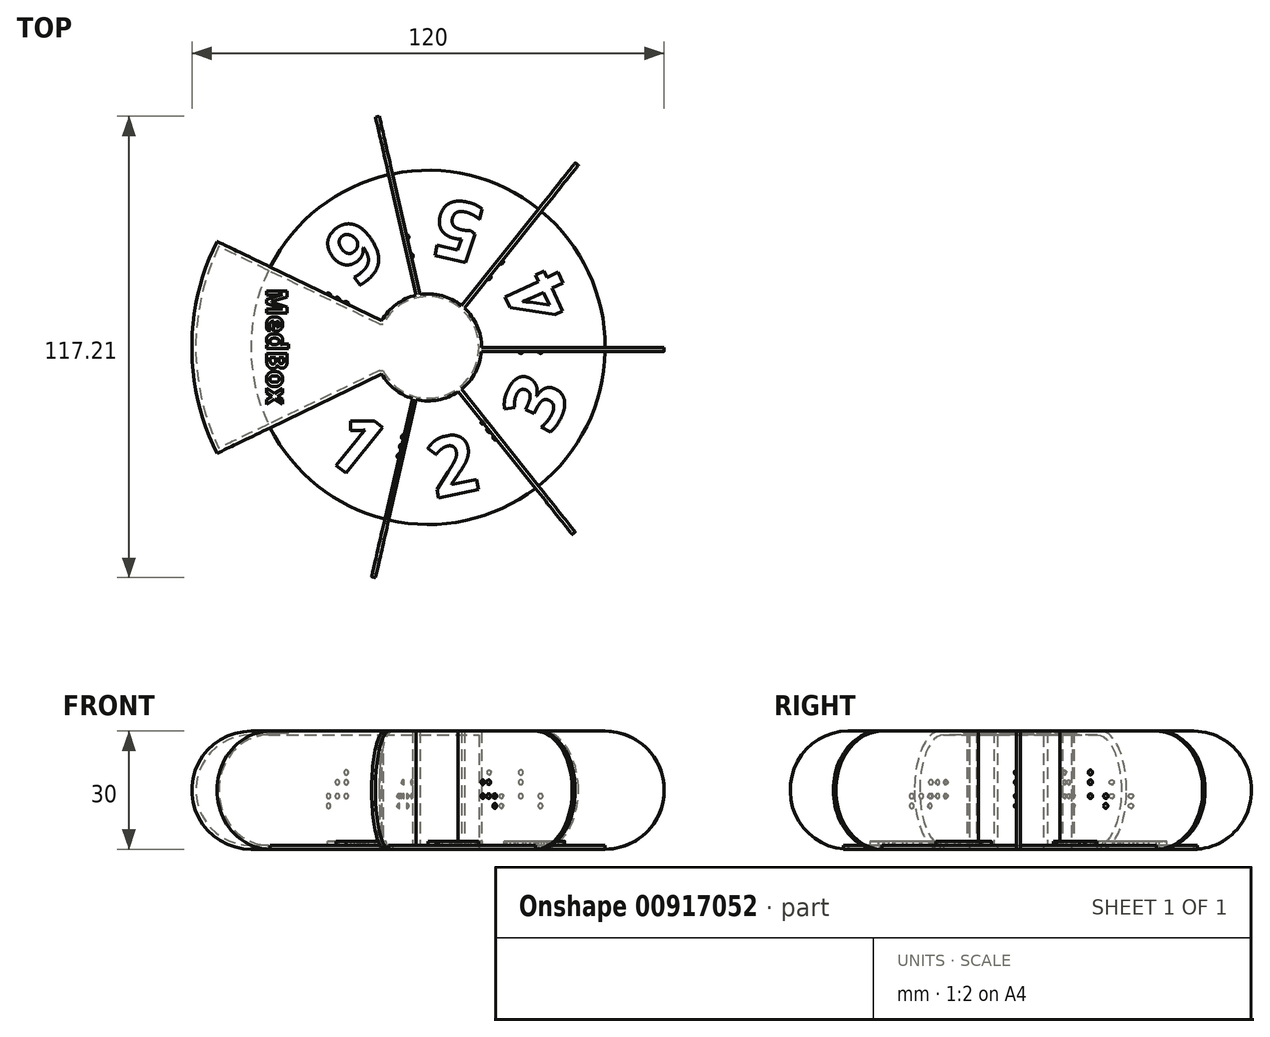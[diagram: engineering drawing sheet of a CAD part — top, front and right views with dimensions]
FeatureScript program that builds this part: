
annotation { "Feature Type Name" : "Feature", "Feature Type Description" : "" }
export const myFeature = defineFeature(function(context is Context, id is Id, definition is map)
    precondition{}
    {
        {
            var Q0;
            Q0=qCreatedBy(makeId("Top.planeOp"),FACE);
            var sketch = newSketch(context, id + "F0", { "sketchPlane" : qUnion([Q0])});
            skCircle(sketch, "E0", {"center": v(0, 0) * mm, "radius": 13.6 * mm});
            skCircle(sketch, "E1", {"center": v(0, 0) * mm, "radius": 60 * mm});
            skLineSegment(sketch, "E2", {"start": v(-3.03, 13.26) * mm, "end": v(-13.35, 58.5) * mm});
            skLineSegment(sketch, "E3", {"start": v(8.48, 10.63) * mm, "end": v(37.4, 46.9) * mm});
            skLineSegment(sketch, "E4", {"start": v(13.6, 0) * mm, "end": v(60, 0) * mm});
            skLineSegment(sketch, "E5", {"start": v(8.48, -10.63) * mm, "end": v(37.4, -46.9) * mm});
            skLineSegment(sketch, "E6", {"start": v(-3.03, -13.26) * mm, "end": v(-13.35, -58.5) * mm});
            skLineSegment(sketch, "E7", {"start": v(-12.25, -5.9) * mm, "end": v(-54.06, -26.03) * mm});
            skLineSegment(sketch, "E8", {"start": v(-12.25, 5.9) * mm, "end": v(-54.06, 26.03) * mm});
            skLineSegment(sketch, "E9", {"start": v(-11.79, 6.79) * mm, "end": v(-53.62, 26.93) * mm});
            skLineSegment(sketch, "E10", {"start": v(-2.04, 13.45) * mm, "end": v(-12.37, 58.71) * mm});
            skLineSegment(sketch, "E11", {"start": v(9.24, 9.98) * mm, "end": v(38.19, 46.28) * mm});
            skLineSegment(sketch, "E12", {"start": v(13.56, -1) * mm, "end": v(60, -1) * mm});
            skLineSegment(sketch, "E13", {"start": v(7.67, -11.23) * mm, "end": v(36.62, -47.53) * mm});
            skLineSegment(sketch, "E14", {"start": v(-4, -13) * mm, "end": v(-14.32, -58.27) * mm});
            skLineSegment(sketch, "E15", {"start": v(-11.79, -6.79) * mm, "end": v(-53.62, -26.93) * mm});
            skSolve(sketch);
        }
        {
            var Q0;
            {var subQ0=sQuery(id+"F0.wireOp",EDGE,"E8");Q0=makeQuery(id+"F0.imprint","IMPRINT",FACE,{"disambiguationData":[TD([[makeQuery(id+"F0.imprint","IMPRINT",EDGE,{"derivedFrom":subQ0}),-1.0]])]});}
            var Q1;
            {var subQ0=sQuery(id+"F0.wireOp",EDGE,"E2");Q1=makeQuery(id+"F0.imprint","IMPRINT",FACE,{"disambiguationData":[TD([[makeQuery(id+"F0.imprint","IMPRINT",EDGE,{"derivedFrom":subQ0}),-1.0]])]});}
            var Q2;
            {var subQ0=sQuery(id+"F0.wireOp",EDGE,"E3");Q2=makeQuery(id+"F0.imprint","IMPRINT",FACE,{"disambiguationData":[TD([[makeQuery(id+"F0.imprint","IMPRINT",EDGE,{"derivedFrom":subQ0}),-1.0]])]});}
            var Q3;
            {var subQ0=sQuery(id+"F0.wireOp",EDGE,"E4");Q3=makeQuery(id+"F0.imprint","IMPRINT",FACE,{"disambiguationData":[TD([[makeQuery(id+"F0.imprint","IMPRINT",EDGE,{"derivedFrom":subQ0}),-1.0]])]});}
            var Q4;
            {var subQ0=sQuery(id+"F0.wireOp",EDGE,"E5");Q4=makeQuery(id+"F0.imprint","IMPRINT",FACE,{"disambiguationData":[TD([[makeQuery(id+"F0.imprint","IMPRINT",EDGE,{"derivedFrom":subQ0}),-1.0]])]});}
            var Q5;
            {var subQ0=sQuery(id+"F0.wireOp",EDGE,"E6");Q5=makeQuery(id+"F0.imprint","IMPRINT",FACE,{"disambiguationData":[TD([[makeQuery(id+"F0.imprint","IMPRINT",EDGE,{"derivedFrom":subQ0}),-1.0]])]});}
            var Q6;
            {var subQ0=sQuery(id+"F0.wireOp",EDGE,"E7");Q6=makeQuery(id+"F0.imprint","IMPRINT",FACE,{"disambiguationData":[TD([[makeQuery(id+"F0.imprint","IMPRINT",EDGE,{"derivedFrom":subQ0}),1.0]])]});}
            var Q7;
            {var subQ0=sQuery(id+"F0.wireOp",EDGE,"E0");var subQ8=makeQuery(id+"F0.imprint","INTERSECT",VERTEX,{"derivedFrom":[subQ0,sQuery(id+"F0.wireOp",EDGE,"E4")]});Q7=makeQuery(id+"F0.imprint","IMPRINT",FACE,{"disambiguationData":[TD([[makeQuery(id+"F0.imprint","IMPRINT",EDGE,{"disambiguationData":[TD([[subQ8,-1.0]])],"derivedFrom":subQ0}),1.0]])]});}
            extrude(context, id + "F1", {"entities" : qUnion([Q0, Q1, Q2, Q3, Q4, Q5, Q6, Q7]), "depth" : 30 * mm, "offsetDistance" : 25 * mm});
        }
        {
            var Q0;
            {var subQ0=sQuery(id+"F0.wireOp",EDGE,"E1");Q0=makeQuery(id+"F1.opExtrude","CAP_EDGE",EDGE,{"disambiguationData":[OSD([subQ0]),TDD([makeQuery(id+"F0.imprint","IMPRINT",EDGE,{"disambiguationData":[TD([[makeQuery(id+"F0.imprint","INTERSECT",VERTEX,{"derivedFrom":[subQ0,sQuery(id+"F0.wireOp",EDGE,"E7")]}),-1.0]])],"derivedFrom":subQ0})])],"isStart":false});}
            var Q1;
            {var subQ0=sQuery(id+"F0.wireOp",EDGE,"E1");Q1=makeQuery(id+"F1.opExtrude","CAP_EDGE",EDGE,{"disambiguationData":[OSD([subQ0]),TDD([makeQuery(id+"F0.imprint","IMPRINT",EDGE,{"disambiguationData":[TD([[makeQuery(id+"F0.imprint","INTERSECT",VERTEX,{"derivedFrom":[subQ0,sQuery(id+"F0.wireOp",EDGE,"E6")]}),1.0]])],"derivedFrom":subQ0})])],"isStart":false});}
            var Q2;
            {var subQ0=sQuery(id+"F0.wireOp",EDGE,"E1");Q2=makeQuery(id+"F1.opExtrude","CAP_EDGE",EDGE,{"disambiguationData":[OSD([subQ0]),TDD([makeQuery(id+"F0.imprint","IMPRINT",EDGE,{"disambiguationData":[TD([[makeQuery(id+"F0.imprint","INTERSECT",VERTEX,{"derivedFrom":[subQ0,sQuery(id+"F0.wireOp",EDGE,"E5")]}),1.0]])],"derivedFrom":subQ0})])],"isStart":false});}
            var Q3;
            {var subQ0=sQuery(id+"F0.wireOp",EDGE,"E1");Q3=makeQuery(id+"F1.opExtrude","CAP_EDGE",EDGE,{"disambiguationData":[OSD([subQ0]),TDD([makeQuery(id+"F0.imprint","IMPRINT",EDGE,{"disambiguationData":[TD([[makeQuery(id+"F0.imprint","INTERSECT",VERTEX,{"derivedFrom":[subQ0,sQuery(id+"F0.wireOp",EDGE,"E4")]}),1.0]])],"derivedFrom":subQ0})])],"isStart":false});}
            var Q4;
            {var subQ0=sQuery(id+"F0.wireOp",EDGE,"E1");Q4=makeQuery(id+"F1.opExtrude","CAP_EDGE",EDGE,{"disambiguationData":[OSD([subQ0]),TDD([makeQuery(id+"F0.imprint","IMPRINT",EDGE,{"disambiguationData":[TD([[makeQuery(id+"F0.imprint","INTERSECT",VERTEX,{"derivedFrom":[subQ0,sQuery(id+"F0.wireOp",EDGE,"E3")]}),1.0]])],"derivedFrom":subQ0})])],"isStart":false});}
            var Q5;
            {var subQ0=sQuery(id+"F0.wireOp",EDGE,"E1");Q5=makeQuery(id+"F1.opExtrude","CAP_EDGE",EDGE,{"disambiguationData":[OSD([subQ0]),TDD([makeQuery(id+"F0.imprint","IMPRINT",EDGE,{"disambiguationData":[TD([[makeQuery(id+"F0.imprint","INTERSECT",VERTEX,{"derivedFrom":[subQ0,sQuery(id+"F0.wireOp",EDGE,"E2")]}),1.0]])],"derivedFrom":subQ0})])],"isStart":false});}
            var Q6;
            {var subQ0=sQuery(id+"F0.wireOp",EDGE,"E1");Q6=makeQuery(id+"F1.opExtrude","CAP_EDGE",EDGE,{"disambiguationData":[OSD([subQ0]),TDD([makeQuery(id+"F0.imprint","IMPRINT",EDGE,{"disambiguationData":[TD([[makeQuery(id+"F0.imprint","INTERSECT",VERTEX,{"derivedFrom":[subQ0,sQuery(id+"F0.wireOp",EDGE,"E8")]}),1.0]])],"derivedFrom":subQ0})])],"isStart":false});}
            var Q7;
            {var subQ0=sQuery(id+"F0.wireOp",EDGE,"E1");Q7=makeQuery(id+"F1.opExtrude","CAP_EDGE",EDGE,{"disambiguationData":[OSD([subQ0]),TDD([makeQuery(id+"F0.imprint","IMPRINT",EDGE,{"disambiguationData":[TD([[makeQuery(id+"F0.imprint","INTERSECT",VERTEX,{"derivedFrom":[subQ0,sQuery(id+"F0.wireOp",EDGE,"E6")]}),1.0]])],"derivedFrom":subQ0})])],"isStart":true});}
            var Q8;
            {var subQ0=sQuery(id+"F0.wireOp",EDGE,"E1");Q8=makeQuery(id+"F1.opExtrude","CAP_EDGE",EDGE,{"disambiguationData":[OSD([subQ0]),TDD([makeQuery(id+"F0.imprint","IMPRINT",EDGE,{"disambiguationData":[TD([[makeQuery(id+"F0.imprint","INTERSECT",VERTEX,{"derivedFrom":[subQ0,sQuery(id+"F0.wireOp",EDGE,"E5")]}),1.0]])],"derivedFrom":subQ0})])],"isStart":true});}
            var Q9;
            {var subQ0=sQuery(id+"F0.wireOp",EDGE,"E1");Q9=makeQuery(id+"F1.opExtrude","CAP_EDGE",EDGE,{"disambiguationData":[OSD([subQ0]),TDD([makeQuery(id+"F0.imprint","IMPRINT",EDGE,{"disambiguationData":[TD([[makeQuery(id+"F0.imprint","INTERSECT",VERTEX,{"derivedFrom":[subQ0,sQuery(id+"F0.wireOp",EDGE,"E7")]}),-1.0]])],"derivedFrom":subQ0})])],"isStart":true});}
            var Q10;
            {var subQ0=sQuery(id+"F0.wireOp",EDGE,"E1");Q10=makeQuery(id+"F1.opExtrude","CAP_EDGE",EDGE,{"disambiguationData":[OSD([subQ0]),TDD([makeQuery(id+"F0.imprint","IMPRINT",EDGE,{"disambiguationData":[TD([[makeQuery(id+"F0.imprint","INTERSECT",VERTEX,{"derivedFrom":[subQ0,sQuery(id+"F0.wireOp",EDGE,"E8")]}),1.0]])],"derivedFrom":subQ0})])],"isStart":true});}
            var Q11;
            {var subQ0=sQuery(id+"F0.wireOp",EDGE,"E1");Q11=makeQuery(id+"F1.opExtrude","CAP_EDGE",EDGE,{"disambiguationData":[OSD([subQ0]),TDD([makeQuery(id+"F0.imprint","IMPRINT",EDGE,{"disambiguationData":[TD([[makeQuery(id+"F0.imprint","INTERSECT",VERTEX,{"derivedFrom":[subQ0,sQuery(id+"F0.wireOp",EDGE,"E4")]}),1.0]])],"derivedFrom":subQ0})])],"isStart":true});}
            var Q12;
            {var subQ0=sQuery(id+"F0.wireOp",EDGE,"E1");Q12=makeQuery(id+"F1.opExtrude","CAP_EDGE",EDGE,{"disambiguationData":[OSD([subQ0]),TDD([makeQuery(id+"F0.imprint","IMPRINT",EDGE,{"disambiguationData":[TD([[makeQuery(id+"F0.imprint","INTERSECT",VERTEX,{"derivedFrom":[subQ0,sQuery(id+"F0.wireOp",EDGE,"E2")]}),1.0]])],"derivedFrom":subQ0})])],"isStart":true});}
            var Q13;
            {var subQ0=sQuery(id+"F0.wireOp",EDGE,"E1");Q13=makeQuery(id+"F1.opExtrude","CAP_EDGE",EDGE,{"disambiguationData":[OSD([subQ0]),TDD([makeQuery(id+"F0.imprint","IMPRINT",EDGE,{"disambiguationData":[TD([[makeQuery(id+"F0.imprint","INTERSECT",VERTEX,{"derivedFrom":[subQ0,sQuery(id+"F0.wireOp",EDGE,"E3")]}),1.0]])],"derivedFrom":subQ0})])],"isStart":true});}
            fillet(context, id + "F2", {"entities" : qUnion([Q0, Q1, Q2, Q3, Q4, Q5, Q6, Q7, Q8, Q9, Q10, Q11, Q12, Q13]), "radius" : 15 * mm, "tangentPropagation" : true, "allowEdgeOverflow" : false});
        }
        {
            var Q0;
            Q0=makeQuery(id+"F1.opExtrude","SWEPT_FACE",FACE,{"disambiguationData":[OSD([sQuery(id+"F0.wireOp",EDGE,"E8")])]});
            var sketch = newSketch(context, id + "F3", { "sketchPlane" : qUnion([Q0])});
            skLineSegment(sketch, "E16", {"start": v(0, 0) * mm, "end": v(0, 50) * mm});
            skLineSegment(sketch, "E17", {"start": v(-13.6, 0) * mm, "end": v(-13.6, 1) * mm});
            skLineSegment(sketch, "E18", {"start": v(-13.6, 30) * mm, "end": v(-13.6, 29) * mm});
            skLineSegment(sketch, "E19", {"start": v(-45, 30) * mm, "end": v(-45, 29) * mm});
            skLineSegment(sketch, "E20", {"start": v(-45, 0) * mm, "end": v(-45, 1) * mm});
            skArc(sketch, "E21", {"start": v(-45, 29) * mm, "mid": v(-59, 15) * mm, "end": v(-45, 1) * mm});
            skLineSegment(sketch, "E22", {"start": v(-45, 29) * mm, "end": v(-13.6, 29) * mm});
            skLineSegment(sketch, "E23", {"start": v(-45, 1) * mm, "end": v(-13.6, 1) * mm});
            skSolve(sketch);
        }
        {
            var Q0;
            Q0=makeQuery(id+"F3.imprint","IMPRINT",FACE,{"disambiguationData":[TD([[makeQuery(id+"F3.imprint","IMPRINT",EDGE,{"derivedFrom":sQuery(id+"F3.wireOp",EDGE,"E18")}),-1.0]])]});
            var Q1;
            Q1=makeQuery(id+"F3.imprint","IMPRINT",FACE,{"disambiguationData":[TD([[makeQuery(id+"F3.imprint","IMPRINT",EDGE,{"derivedFrom":sQuery(id+"F3.wireOp",EDGE,"E19")}),-1.0]])]});
            var Q2;
            Q2=sQuery(id+"F3.wireOp",EDGE,"E16");
            revolve(context, id + "F4", {"operationType" : NewBodyOperationType.ADD, "surfaceOperationType" : NewSurfaceOperationType.NEW, "entities" : qUnion([Q0, Q1]), "axis" : qUnion([Q2]), "revolveType" : RevolveType.ONE_DIRECTION, "angle" : 52 * degree});
        }
        {
            var Q0;
            Q0=makeQuery(id+"F1.opExtrude","CAP_FACE",FACE,{"disambiguationData":[OSD([sQuery(id+"F0.wireOp",EDGE,"E0"),sQuery(id+"F0.wireOp",EDGE,"E1"),sQuery(id+"F0.wireOp",EDGE,"E2"),sQuery(id+"F0.wireOp",EDGE,"E3"),sQuery(id+"F0.wireOp",EDGE,"E4"),sQuery(id+"F0.wireOp",EDGE,"E5"),sQuery(id+"F0.wireOp",EDGE,"E6"),sQuery(id+"F0.wireOp",EDGE,"E7"),sQuery(id+"F0.wireOp",EDGE,"E8"),sQuery(id+"F0.wireOp",EDGE,"E9"),sQuery(id+"F0.wireOp",EDGE,"E10"),sQuery(id+"F0.wireOp",EDGE,"E11"),sQuery(id+"F0.wireOp",EDGE,"E12"),sQuery(id+"F0.wireOp",EDGE,"E13"),sQuery(id+"F0.wireOp",EDGE,"E14"),sQuery(id+"F0.wireOp",EDGE,"E15")])],"isStart":true});
            var sketch = newSketch(context, id + "F5", { "sketchPlane" : qUnion([Q0])});
            skCircle(sketch, "E24", {"center": v(0, 0) * mm, "radius": 12.9 * mm});
            skLineSegment(sketch, "E25", {"start": v(-12.25, 5.9) * mm, "end": v(-11.47, 5.9) * mm});
            skLineSegment(sketch, "E26", {"start": v(-12.25, -5.9) * mm, "end": v(-11.47, -5.9) * mm});
            skSolve(sketch);
        }
        {
            var Q0;
            {var subQ0=sQuery(id+"F5.wireOp",EDGE,"E24");var subQ1=makeQuery(id+"F5.imprint","INTERSECT",VERTEX,{"derivedFrom":[subQ0,sQuery(id+"F5.wireOp",EDGE,"E25")]});Q0=makeQuery(id+"F5.imprint","IMPRINT",FACE,{"disambiguationData":[TD([[makeQuery(id+"F5.imprint","IMPRINT",EDGE,{"disambiguationData":[TD([[subQ1,-1.0]])],"derivedFrom":subQ0}),1.0]])]});}
            var Q1;
            {var subQ0=sQuery(id+"F5.wireOp",EDGE,"E25");Q1=makeQuery(id+"F5.imprint","IMPRINT",FACE,{"disambiguationData":[TD([[makeQuery(id+"F5.imprint","IMPRINT",EDGE,{"derivedFrom":subQ0}),-1.0]])]});}
            extrude(context, id + "F6", {"entities" : qUnion([Q0, Q1]), "operationType" : NewBodyOperationType.REMOVE, "oppositeDirection" : true, "depth" : 29 * mm, "offsetDistance" : 25 * mm});
        }
        {
            var Q0;
            Q0=makeQuery(id+"F1.opExtrude","CAP_FACE",FACE,{"disambiguationData":[OSD([sQuery(id+"F0.wireOp",EDGE,"E0"),sQuery(id+"F0.wireOp",EDGE,"E1"),sQuery(id+"F0.wireOp",EDGE,"E2"),sQuery(id+"F0.wireOp",EDGE,"E3"),sQuery(id+"F0.wireOp",EDGE,"E4"),sQuery(id+"F0.wireOp",EDGE,"E5"),sQuery(id+"F0.wireOp",EDGE,"E6"),sQuery(id+"F0.wireOp",EDGE,"E7"),sQuery(id+"F0.wireOp",EDGE,"E8"),sQuery(id+"F0.wireOp",EDGE,"E9"),sQuery(id+"F0.wireOp",EDGE,"E10"),sQuery(id+"F0.wireOp",EDGE,"E11"),sQuery(id+"F0.wireOp",EDGE,"E12"),sQuery(id+"F0.wireOp",EDGE,"E13"),sQuery(id+"F0.wireOp",EDGE,"E14"),sQuery(id+"F0.wireOp",EDGE,"E15")])],"isStart":true});
            var sketch = newSketch(context, id + "F7", { "sketchPlane" : qUnion([Q0])});
            skArc(sketch, "E27", {"start": v(-40.54, 19.52) * mm, "mid": v(45, 0) * mm, "end": v(-40.54, -19.52) * mm});
            skSolve(sketch);
        }
        {
            var Q0;
            {var subQ3=sQuery(id+"F0.wireOp",EDGE,"E14");var subQ4=makeQuery(id+"F1.opExtrude","CAP_EDGE",EDGE,{"disambiguationData":[OSD([subQ3])],"isStart":true});Q0=makeQuery(id+"F7.imprint","IMPRINT",FACE,{"disambiguationData":[TD([[makeQuery(id+"F7.imprint","IMPRINT",EDGE,{"derivedFrom":subQ4}),1.0]])]});}
            var Q1;
            {var subQ1=sQuery(id+"F0.wireOp",EDGE,"E6");var subQ2=makeQuery(id+"F1.opExtrude","CAP_EDGE",EDGE,{"disambiguationData":[OSD([subQ1])],"isStart":true});Q1=makeQuery(id+"F7.imprint","IMPRINT",FACE,{"disambiguationData":[TD([[makeQuery(id+"F7.imprint","IMPRINT",EDGE,{"derivedFrom":subQ2}),-1.0]])]});}
            var Q2;
            {var subQ1=sQuery(id+"F0.wireOp",EDGE,"E5");var subQ2=makeQuery(id+"F1.opExtrude","CAP_EDGE",EDGE,{"disambiguationData":[OSD([subQ1])],"isStart":true});Q2=makeQuery(id+"F7.imprint","IMPRINT",FACE,{"disambiguationData":[TD([[makeQuery(id+"F7.imprint","IMPRINT",EDGE,{"derivedFrom":subQ2}),-1.0]])]});}
            var Q3;
            {var subQ3=sQuery(id+"F0.wireOp",EDGE,"E4");var subQ4=makeQuery(id+"F1.opExtrude","CAP_EDGE",EDGE,{"disambiguationData":[OSD([subQ3])],"isStart":true});Q3=makeQuery(id+"F7.imprint","IMPRINT",FACE,{"disambiguationData":[TD([[makeQuery(id+"F7.imprint","IMPRINT",EDGE,{"derivedFrom":subQ4}),-1.0]])]});}
            var Q4;
            {var subQ1=sQuery(id+"F0.wireOp",EDGE,"E3");var subQ2=makeQuery(id+"F1.opExtrude","CAP_EDGE",EDGE,{"disambiguationData":[OSD([subQ1])],"isStart":true});Q4=makeQuery(id+"F7.imprint","IMPRINT",FACE,{"disambiguationData":[TD([[makeQuery(id+"F7.imprint","IMPRINT",EDGE,{"derivedFrom":subQ2}),-1.0]])]});}
            var Q5;
            {var subQ1=sQuery(id+"F0.wireOp",EDGE,"E2");var subQ2=makeQuery(id+"F1.opExtrude","CAP_EDGE",EDGE,{"disambiguationData":[OSD([subQ1])],"isStart":true});Q5=makeQuery(id+"F7.imprint","IMPRINT",FACE,{"disambiguationData":[TD([[makeQuery(id+"F7.imprint","IMPRINT",EDGE,{"derivedFrom":subQ2}),-1.0]])]});}
            extrude(context, id + "F8", {"entities" : qUnion([Q0, Q1, Q2, Q3, Q4, Q5]), "operationType" : NewBodyOperationType.ADD, "oppositeDirection" : true, "depth" : 1 * mm, "offsetDistance" : 25 * mm});
        }
        {
            var Q0;
            Q0=makeQuery(id+"F8.opExtrude","CAP_FACE",FACE,{"disambiguationData":[OSD([sQuery(id+"F0.wireOp",EDGE,"E0"),sQuery(id+"F0.wireOp",EDGE,"E14"),sQuery(id+"F0.wireOp",EDGE,"E15"),sQuery(id+"F7.wireOp",EDGE,"E27")])],"isStart":false});
            var sketch = newSketch(context, id + "F9", { "sketchPlane" : qUnion([Q0])});
            skCircle(sketch, "E28", {"center": v(0, 0) * mm, "radius": 23 * mm});
            skLineSegment(sketch, "E29", {"start": v(0, 0) * mm, "end": v(40.32, -19.97) * mm});
            skLineSegment(sketch, "E30", {"start": v(0, 0) * mm, "end": v(40.76, 19.07) * mm});
            skLineSegment(sketch, "E31", {"start": v(0, 0) * mm, "end": v(10.5, 43.76) * mm});
            skLineSegment(sketch, "E32", {"start": v(0, 0) * mm, "end": v(-27.66, 35.5) * mm});
            skLineSegment(sketch, "E33", {"start": v(0, 0) * mm, "end": v(9.53, -43.98) * mm});
            skText(sketch, "E34", { "text": "2", "fontName": "OpenSans-Bold.ttf"});
            skLineSegment(sketch, "E35", {"start": v(0, 0) * mm, "end": v(-28.06, -35.18) * mm});
            skText(sketch, "E36", { "text": "1", "fontName": "OpenSans-Bold.ttf"});
            skText(sketch, "E37", { "text": "3", "fontName": "OpenSans-Bold.ttf"});
            skText(sketch, "E38", { "text": "4", "fontName": "OpenSans-Bold.ttf"});
            skText(sketch, "E39", { "text": "5", "fontName": "OpenSans-Bold.ttf"});
            skText(sketch, "E40", { "text": "6", "fontName": "OpenSans-Bold.ttf"});
            const initialGuessF9  = {"E34": [0.0019, -0.03847, 0.97734, 0.21167, 0.015], "E36": [-0.02759, -0.0266, 0.78183, -0.62349, 0.015], "E37": [0.0313, -0.02244, 0.44387, 0.8961, 0.015], "E38": [0.03716, 0.01026, -0.42385, 0.90573, 0.015], "E39": [0.01485, 0.03552, -0.9724, 0.23334, 0.015], "E40": [-0.0184, 0.03384, -0.78871, -0.61476, 0.015]};
            skSetInitialGuess(sketch, initialGuessF9);
            skSolve(sketch);
        }
        {
            var Q0;
            {var subQ0=sQuery(id+"F9.wireOp",EDGE,"E39.sketch_text.stroke-4");Q0=makeQuery(id+"F9.imprint","IMPRINT",FACE,{"disambiguationData":[TD([[makeQuery(id+"F9.imprint","IMPRINT",EDGE,{"derivedFrom":subQ0}),-1.0]])]});}
            var Q1;
            {var subQ5=sQuery(id+"F9.wireOp",EDGE,"E39.sketch_text.stroke-0");Q1=makeQuery(id+"F9.imprint","IMPRINT",FACE,{"disambiguationData":[TD([[makeQuery(id+"F9.imprint","IMPRINT",EDGE,{"derivedFrom":subQ5}),-1.0]])]});}
            var Q2;
            {var subQ11=sQuery(id+"F9.wireOp",EDGE,"E39.sketch_text.stroke-10");Q2=makeQuery(id+"F9.imprint","IMPRINT",FACE,{"disambiguationData":[TD([[makeQuery(id+"F9.imprint","IMPRINT",EDGE,{"derivedFrom":subQ11}),-1.0]])]});}
            var Q3;
            {var subQ5=sQuery(id+"F9.wireOp",EDGE,"E39.sketch_text.stroke-15");Q3=makeQuery(id+"F9.imprint","IMPRINT",FACE,{"disambiguationData":[TD([[makeQuery(id+"F9.imprint","IMPRINT",EDGE,{"derivedFrom":subQ5}),-1.0]])]});}
            var Q4;
            Q4=makeQuery(id+"F9.imprint","IMPRINT",FACE,{"disambiguationData":[TD([[makeQuery(id+"F9.imprint","IMPRINT",EDGE,{"derivedFrom":sQuery(id+"F9.wireOp",EDGE,"E38.sketch_text.stroke-0")}),-1.0]])]});
            var Q5;
            {var subQ0=sQuery(id+"F9.wireOp",EDGE,"E38.sketch_text.stroke-5");Q5=makeQuery(id+"F9.imprint","IMPRINT",FACE,{"disambiguationData":[TD([[makeQuery(id+"F9.imprint","IMPRINT",EDGE,{"derivedFrom":subQ0}),-1.0]])]});}
            var Q6;
            Q6=makeQuery(id+"F9.imprint","IMPRINT",FACE,{"disambiguationData":[TD([[makeQuery(id+"F9.imprint","IMPRINT",EDGE,{"derivedFrom":sQuery(id+"F9.wireOp",EDGE,"E37.sketch_text.stroke-0")}),-1.0]])]});
            var Q7;
            {var subQ0=sQuery(id+"F9.wireOp",EDGE,"E37.sketch_text.stroke-21");Q7=makeQuery(id+"F9.imprint","IMPRINT",FACE,{"disambiguationData":[TD([[makeQuery(id+"F9.imprint","IMPRINT",EDGE,{"derivedFrom":subQ0}),-1.0]])]});}
            var Q8;
            {var subQ0=sQuery(id+"F9.wireOp",EDGE,"E37.sketch_text.stroke-15");Q8=makeQuery(id+"F9.imprint","IMPRINT",FACE,{"disambiguationData":[TD([[makeQuery(id+"F9.imprint","IMPRINT",EDGE,{"derivedFrom":subQ0}),-1.0]])]});}
            var Q9;
            {var subQ0=sQuery(id+"F9.wireOp",EDGE,"E37.sketch_text.stroke-7");Q9=makeQuery(id+"F9.imprint","IMPRINT",FACE,{"disambiguationData":[TD([[makeQuery(id+"F9.imprint","IMPRINT",EDGE,{"derivedFrom":subQ0}),-1.0]])]});}
            var Q10;
            {var subQ0=sQuery(id+"F9.wireOp",EDGE,"E34.sketch_text.stroke-1");Q10=makeQuery(id+"F9.imprint","IMPRINT",FACE,{"disambiguationData":[TD([[makeQuery(id+"F9.imprint","IMPRINT",EDGE,{"derivedFrom":subQ0}),-1.0]])]});}
            var Q11;
            {var subQ5=sQuery(id+"F9.wireOp",EDGE,"E34.sketch_text.stroke-23");Q11=makeQuery(id+"F9.imprint","IMPRINT",FACE,{"disambiguationData":[TD([[makeQuery(id+"F9.imprint","IMPRINT",EDGE,{"derivedFrom":subQ5}),-1.0]])]});}
            var Q12;
            {var subQ13=sQuery(id+"F9.wireOp",EDGE,"E34.sketch_text.stroke-4");Q12=makeQuery(id+"F9.imprint","IMPRINT",FACE,{"disambiguationData":[TD([[makeQuery(id+"F9.imprint","IMPRINT",EDGE,{"derivedFrom":subQ13}),-1.0]])]});}
            var Q13;
            {var subQ0=sQuery(id+"F9.wireOp",EDGE,"E34.sketch_text.stroke-8");Q13=makeQuery(id+"F9.imprint","IMPRINT",FACE,{"disambiguationData":[TD([[makeQuery(id+"F9.imprint","IMPRINT",EDGE,{"derivedFrom":subQ0}),-1.0]])]});}
            var Q14;
            {var subQ1=sQuery(id+"F9.wireOp",EDGE,"E36.sketch_text.stroke-5");Q14=makeQuery(id+"F9.imprint","IMPRINT",FACE,{"disambiguationData":[TD([[makeQuery(id+"F9.imprint","IMPRINT",EDGE,{"derivedFrom":subQ1}),-1.0]])]});}
            var Q15;
            Q15=makeQuery(id+"F9.imprint","IMPRINT",FACE,{"disambiguationData":[TD([[makeQuery(id+"F9.imprint","IMPRINT",EDGE,{"derivedFrom":sQuery(id+"F9.wireOp",EDGE,"E36.sketch_text.stroke-0")}),-1.0]])]});
            var Q16;
            {var subQ11=sQuery(id+"F9.wireOp",EDGE,"E40.sketch_text.stroke-0");Q16=makeQuery(id+"F9.imprint","IMPRINT",FACE,{"disambiguationData":[TD([[makeQuery(id+"F9.imprint","IMPRINT",EDGE,{"derivedFrom":subQ11}),-1.0]])]});}
            var Q17;
            {var subQ8=sQuery(id+"F9.wireOp",EDGE,"E40.sketch_text.stroke-10");Q17=makeQuery(id+"F9.imprint","IMPRINT",FACE,{"disambiguationData":[TD([[makeQuery(id+"F9.imprint","IMPRINT",EDGE,{"derivedFrom":subQ8}),-1.0]])]});}
            var Q18;
            {var subQ0=sQuery(id+"F9.wireOp",EDGE,"E40.sketch_text.stroke-2");Q18=makeQuery(id+"F9.imprint","IMPRINT",FACE,{"disambiguationData":[TD([[makeQuery(id+"F9.imprint","IMPRINT",EDGE,{"derivedFrom":subQ0}),-1.0]])]});}
            extrude(context, id + "F10", {"entities" : qUnion([Q0, Q1, Q2, Q3, Q4, Q5, Q6, Q7, Q8, Q9, Q10, Q11, Q12, Q13, Q14, Q15, Q16, Q17, Q18]), "operationType" : NewBodyOperationType.ADD, "depth" : 1 * mm, "offsetDistance" : 25 * mm});
        }
        {
            var Q0;
            Q0=makeQuery(id+"F1.opExtrude","SWEPT_FACE",FACE,{"disambiguationData":[OSD([sQuery(id+"F0.wireOp",EDGE,"E14")])]});
            var sketch = newSketch(context, id + "F11", { "sketchPlane" : qUnion([Q0])});
            skLineSegment(sketch, "E41", {"start": v(23.56, 19.5) * mm, "end": v(23.56, 11) * mm});
            skLineSegment(sketch, "E42", {"start": v(23.56, 11) * mm, "end": v(28.56, 11) * mm});
            skCircle(sketch, "E43", {"center": v(23.56, 11) * mm, "radius": 0.6 * mm});
            skPoint(sketch, "E44", {"position": v(23.56, 13.5) * mm});
            skCircle(sketch, "E45", {"center": v(23.56, 13.5) * mm, "radius": 0.6 * mm});
            skPoint(sketch, "E46", {"position": v(23.56, 17) * mm});
            skCircle(sketch, "E47", {"center": v(23.56, 17) * mm, "radius": 0.6 * mm});
            skCircle(sketch, "E48", {"center": v(23.56, 19.5) * mm, "radius": 0.6 * mm});
            skPoint(sketch, "E49", {"position": v(26.06, 11) * mm});
            skCircle(sketch, "E50", {"center": v(26.06, 11) * mm, "radius": 0.6 * mm});
            skCircle(sketch, "E51", {"center": v(28.56, 11) * mm, "radius": 0.6 * mm});
            skLineSegment(sketch, "E52", {"start": v(23.56, 13.5) * mm, "end": v(28.56, 13.5) * mm});
            skCircle(sketch, "E53", {"center": v(26.06, 13.5) * mm, "radius": 0.6 * mm});
            skCircle(sketch, "E54", {"center": v(28.56, 13.5) * mm, "radius": 0.6 * mm});
            skLineSegment(sketch, "E55", {"start": v(23.56, 17) * mm, "end": v(28.56, 17) * mm});
            skCircle(sketch, "E56", {"center": v(26.06, 17) * mm, "radius": 0.6 * mm});
            skCircle(sketch, "E57", {"center": v(28.56, 17) * mm, "radius": 0.6 * mm});
            skLineSegment(sketch, "E58", {"start": v(23.56, 19.5) * mm, "end": v(28.56, 19.5) * mm});
            skCircle(sketch, "E59", {"center": v(26.06, 19.5) * mm, "radius": 0.6 * mm});
            skCircle(sketch, "E60", {"center": v(28.56, 19.5) * mm, "radius": 0.6 * mm});
            skSolve(sketch);
        }
        {
            var Q0;
            Q0=makeQuery(id+"F1.opExtrude","SWEPT_FACE",FACE,{"disambiguationData":[OSD([sQuery(id+"F0.wireOp",EDGE,"E13")])]});
            var sketch = newSketch(context, id + "F12", { "sketchPlane" : qUnion([Q0])});
            skLineSegment(sketch, "E61", {"start": v(23.56, 19.5) * mm, "end": v(23.56, 11) * mm});
            skLineSegment(sketch, "E62", {"start": v(23.56, 11) * mm, "end": v(28.56, 11) * mm});
            skCircle(sketch, "E63", {"center": v(23.56, 11) * mm, "radius": 0.6 * mm});
            skPoint(sketch, "E64", {"position": v(23.56, 13.5) * mm});
            skCircle(sketch, "E65", {"center": v(23.56, 13.5) * mm, "radius": 0.6 * mm});
            skPoint(sketch, "E66", {"position": v(23.56, 17) * mm});
            skCircle(sketch, "E67", {"center": v(23.56, 17) * mm, "radius": 0.6 * mm});
            skCircle(sketch, "E68", {"center": v(23.56, 19.5) * mm, "radius": 0.6 * mm});
            skPoint(sketch, "E69", {"position": v(26.06, 11) * mm});
            skCircle(sketch, "E70", {"center": v(26.06, 11) * mm, "radius": 0.6 * mm});
            skCircle(sketch, "E71", {"center": v(28.56, 11) * mm, "radius": 0.6 * mm});
            skLineSegment(sketch, "E72", {"start": v(23.56, 13.5) * mm, "end": v(28.56, 13.5) * mm});
            skCircle(sketch, "E73", {"center": v(26.06, 13.5) * mm, "radius": 0.6 * mm});
            skCircle(sketch, "E74", {"center": v(28.56, 13.5) * mm, "radius": 0.6 * mm});
            skLineSegment(sketch, "E75", {"start": v(23.56, 17) * mm, "end": v(28.56, 17) * mm});
            skCircle(sketch, "E76", {"center": v(26.06, 17) * mm, "radius": 0.6 * mm});
            skCircle(sketch, "E77", {"center": v(28.56, 17) * mm, "radius": 0.6 * mm});
            skLineSegment(sketch, "E78", {"start": v(23.56, 19.5) * mm, "end": v(28.56, 19.5) * mm});
            skCircle(sketch, "E79", {"center": v(26.06, 19.5) * mm, "radius": 0.6 * mm});
            skCircle(sketch, "E80", {"center": v(28.56, 19.5) * mm, "radius": 0.6 * mm});
            skSolve(sketch);
        }
        {
            var Q0;
            Q0=makeQuery(id+"F1.opExtrude","SWEPT_FACE",FACE,{"disambiguationData":[OSD([sQuery(id+"F0.wireOp",EDGE,"E12")])]});
            var sketch = newSketch(context, id + "F13", { "sketchPlane" : qUnion([Q0])});
            skLineSegment(sketch, "E81", {"start": v(23.56, 19.5) * mm, "end": v(23.56, 11) * mm});
            skLineSegment(sketch, "E82", {"start": v(23.56, 11) * mm, "end": v(28.56, 11) * mm});
            skCircle(sketch, "E83", {"center": v(23.56, 11) * mm, "radius": 0.6 * mm});
            skPoint(sketch, "E84", {"position": v(23.56, 13.5) * mm});
            skCircle(sketch, "E85", {"center": v(23.56, 13.5) * mm, "radius": 0.6 * mm});
            skPoint(sketch, "E86", {"position": v(23.56, 17) * mm});
            skCircle(sketch, "E87", {"center": v(23.56, 17) * mm, "radius": 0.6 * mm});
            skCircle(sketch, "E88", {"center": v(23.56, 19.5) * mm, "radius": 0.6 * mm});
            skPoint(sketch, "E89", {"position": v(26.06, 11) * mm});
            skCircle(sketch, "E90", {"center": v(26.06, 11) * mm, "radius": 0.6 * mm});
            skCircle(sketch, "E91", {"center": v(28.56, 11) * mm, "radius": 0.6 * mm});
            skLineSegment(sketch, "E92", {"start": v(23.56, 13.5) * mm, "end": v(28.56, 13.5) * mm});
            skCircle(sketch, "E93", {"center": v(26.06, 13.5) * mm, "radius": 0.6 * mm});
            skCircle(sketch, "E94", {"center": v(28.56, 13.5) * mm, "radius": 0.6 * mm});
            skLineSegment(sketch, "E95", {"start": v(23.56, 17) * mm, "end": v(28.56, 17) * mm});
            skCircle(sketch, "E96", {"center": v(26.06, 17) * mm, "radius": 0.6 * mm});
            skCircle(sketch, "E97", {"center": v(28.56, 17) * mm, "radius": 0.6 * mm});
            skLineSegment(sketch, "E98", {"start": v(23.56, 19.5) * mm, "end": v(28.56, 19.5) * mm});
            skCircle(sketch, "E99", {"center": v(26.06, 19.5) * mm, "radius": 0.6 * mm});
            skCircle(sketch, "E100", {"center": v(28.56, 19.5) * mm, "radius": 0.6 * mm});
            skSolve(sketch);
        }
        {
            var Q0;
            Q0=makeQuery(id+"F1.opExtrude","SWEPT_FACE",FACE,{"disambiguationData":[OSD([sQuery(id+"F0.wireOp",EDGE,"E11")])]});
            var sketch = newSketch(context, id + "F14", { "sketchPlane" : qUnion([Q0])});
            skLineSegment(sketch, "E101", {"start": v(23.56, 19.5) * mm, "end": v(23.56, 11) * mm});
            skLineSegment(sketch, "E102", {"start": v(23.56, 11) * mm, "end": v(28.56, 11) * mm});
            skCircle(sketch, "E103", {"center": v(23.56, 11) * mm, "radius": 0.6 * mm});
            skPoint(sketch, "E104", {"position": v(23.56, 13.5) * mm});
            skCircle(sketch, "E105", {"center": v(23.56, 13.5) * mm, "radius": 0.6 * mm});
            skPoint(sketch, "E106", {"position": v(23.56, 17) * mm});
            skCircle(sketch, "E107", {"center": v(23.56, 17) * mm, "radius": 0.6 * mm});
            skCircle(sketch, "E108", {"center": v(23.56, 19.5) * mm, "radius": 0.6 * mm});
            skPoint(sketch, "E109", {"position": v(26.06, 11) * mm});
            skCircle(sketch, "E110", {"center": v(26.06, 11) * mm, "radius": 0.6 * mm});
            skCircle(sketch, "E111", {"center": v(28.56, 11) * mm, "radius": 0.6 * mm});
            skLineSegment(sketch, "E112", {"start": v(23.56, 13.5) * mm, "end": v(28.56, 13.5) * mm});
            skCircle(sketch, "E113", {"center": v(26.06, 13.5) * mm, "radius": 0.6 * mm});
            skCircle(sketch, "E114", {"center": v(28.56, 13.5) * mm, "radius": 0.6 * mm});
            skLineSegment(sketch, "E115", {"start": v(23.56, 17) * mm, "end": v(28.56, 17) * mm});
            skCircle(sketch, "E116", {"center": v(26.06, 17) * mm, "radius": 0.6 * mm});
            skCircle(sketch, "E117", {"center": v(28.56, 17) * mm, "radius": 0.6 * mm});
            skLineSegment(sketch, "E118", {"start": v(23.56, 19.5) * mm, "end": v(28.56, 19.5) * mm});
            skCircle(sketch, "E119", {"center": v(26.06, 19.5) * mm, "radius": 0.6 * mm});
            skCircle(sketch, "E120", {"center": v(28.56, 19.5) * mm, "radius": 0.6 * mm});
            skSolve(sketch);
        }
        {
            var Q0;
            Q0=makeQuery(id+"F1.opExtrude","SWEPT_FACE",FACE,{"disambiguationData":[OSD([sQuery(id+"F0.wireOp",EDGE,"E10")])]});
            var sketch = newSketch(context, id + "F15", { "sketchPlane" : qUnion([Q0])});
            skLineSegment(sketch, "E121", {"start": v(23.56, 19.5) * mm, "end": v(23.56, 11) * mm});
            skLineSegment(sketch, "E122", {"start": v(23.56, 11) * mm, "end": v(28.56, 11) * mm});
            skCircle(sketch, "E123", {"center": v(23.56, 11) * mm, "radius": 0.6 * mm});
            skPoint(sketch, "E124", {"position": v(23.56, 13.5) * mm});
            skCircle(sketch, "E125", {"center": v(23.56, 13.5) * mm, "radius": 0.6 * mm});
            skPoint(sketch, "E126", {"position": v(23.56, 17) * mm});
            skCircle(sketch, "E127", {"center": v(23.56, 17) * mm, "radius": 0.6 * mm});
            skCircle(sketch, "E128", {"center": v(23.56, 19.5) * mm, "radius": 0.6 * mm});
            skPoint(sketch, "E129", {"position": v(26.06, 11) * mm});
            skCircle(sketch, "E130", {"center": v(26.06, 11) * mm, "radius": 0.6 * mm});
            skCircle(sketch, "E131", {"center": v(28.56, 11) * mm, "radius": 0.6 * mm});
            skLineSegment(sketch, "E132", {"start": v(23.56, 13.5) * mm, "end": v(28.56, 13.5) * mm});
            skCircle(sketch, "E133", {"center": v(26.06, 13.5) * mm, "radius": 0.6 * mm});
            skCircle(sketch, "E134", {"center": v(28.56, 13.5) * mm, "radius": 0.6 * mm});
            skLineSegment(sketch, "E135", {"start": v(23.56, 17) * mm, "end": v(28.56, 17) * mm});
            skCircle(sketch, "E136", {"center": v(26.06, 17) * mm, "radius": 0.6 * mm});
            skCircle(sketch, "E137", {"center": v(28.56, 17) * mm, "radius": 0.6 * mm});
            skLineSegment(sketch, "E138", {"start": v(23.56, 19.5) * mm, "end": v(28.56, 19.5) * mm});
            skCircle(sketch, "E139", {"center": v(26.06, 19.5) * mm, "radius": 0.6 * mm});
            skCircle(sketch, "E140", {"center": v(28.56, 19.5) * mm, "radius": 0.6 * mm});
            skSolve(sketch);
        }
        {
            var Q0;
            Q0=makeQuery(id+"F1.opExtrude","SWEPT_FACE",FACE,{"disambiguationData":[OSD([sQuery(id+"F0.wireOp",EDGE,"E9")])]});
            var sketch = newSketch(context, id + "F16", { "sketchPlane" : qUnion([Q0])});
            skLineSegment(sketch, "E141", {"start": v(23.56, 19.5) * mm, "end": v(23.56, 11) * mm});
            skLineSegment(sketch, "E142", {"start": v(23.56, 11) * mm, "end": v(28.56, 11) * mm});
            skCircle(sketch, "E143", {"center": v(23.56, 11) * mm, "radius": 0.6 * mm});
            skPoint(sketch, "E144", {"position": v(23.56, 13.5) * mm});
            skCircle(sketch, "E145", {"center": v(23.56, 13.5) * mm, "radius": 0.6 * mm});
            skPoint(sketch, "E146", {"position": v(23.56, 17) * mm});
            skCircle(sketch, "E147", {"center": v(23.56, 17) * mm, "radius": 0.6 * mm});
            skCircle(sketch, "E148", {"center": v(23.56, 19.5) * mm, "radius": 0.6 * mm});
            skPoint(sketch, "E149", {"position": v(26.06, 11) * mm});
            skCircle(sketch, "E150", {"center": v(26.06, 11) * mm, "radius": 0.6 * mm});
            skCircle(sketch, "E151", {"center": v(28.56, 11) * mm, "radius": 0.6 * mm});
            skLineSegment(sketch, "E152", {"start": v(23.56, 13.5) * mm, "end": v(28.56, 13.5) * mm});
            skCircle(sketch, "E153", {"center": v(26.06, 13.5) * mm, "radius": 0.6 * mm});
            skCircle(sketch, "E154", {"center": v(28.56, 13.5) * mm, "radius": 0.6 * mm});
            skLineSegment(sketch, "E155", {"start": v(23.56, 17) * mm, "end": v(28.56, 17) * mm});
            skCircle(sketch, "E156", {"center": v(26.06, 17) * mm, "radius": 0.6 * mm});
            skCircle(sketch, "E157", {"center": v(28.56, 17) * mm, "radius": 0.6 * mm});
            skLineSegment(sketch, "E158", {"start": v(23.56, 19.5) * mm, "end": v(28.56, 19.5) * mm});
            skCircle(sketch, "E159", {"center": v(26.06, 19.5) * mm, "radius": 0.6 * mm});
            skCircle(sketch, "E160", {"center": v(28.56, 19.5) * mm, "radius": 0.6 * mm});
            skSolve(sketch);
        }
        {
            var Q0;
            {var subQ0=sQuery(id+"F11.wireOp",EDGE,"E41");var subQ1=makeQuery(id+"F11.imprint","INTERSECT",VERTEX,{"derivedFrom":[subQ0,sQuery(id+"F11.wireOp",EDGE,"E52")]});Q0=makeQuery(id+"F11.imprint","IMPRINT",FACE,{"disambiguationData":[TD([[makeQuery(id+"F11.imprint","IMPRINT",EDGE,{"disambiguationData":[TD([[subQ1,1.0]])],"derivedFrom":subQ0}),-1.0]])]});}
            var Q1;
            {var subQ0=sQuery(id+"F11.wireOp",EDGE,"E52");var subQ1=sQuery(id+"F11.wireOp",EDGE,"E41");var subQ2=makeQuery(id+"F11.imprint","INTERSECT",VERTEX,{"derivedFrom":[subQ1,subQ0]});Q1=makeQuery(id+"F11.imprint","IMPRINT",FACE,{"disambiguationData":[TD([[makeQuery(id+"F11.imprint","IMPRINT",EDGE,{"disambiguationData":[TD([[subQ2,1.0]])],"derivedFrom":subQ1}),1.0]])]});}
            var Q2;
            {var subQ0=sQuery(id+"F11.wireOp",EDGE,"E52");var subQ1=sQuery(id+"F11.wireOp",EDGE,"E41");var subQ2=makeQuery(id+"F11.imprint","INTERSECT",VERTEX,{"derivedFrom":[subQ1,subQ0]});Q2=makeQuery(id+"F11.imprint","IMPRINT",FACE,{"disambiguationData":[TD([[makeQuery(id+"F11.imprint","IMPRINT",EDGE,{"disambiguationData":[TD([[subQ2,-1.0]])],"derivedFrom":subQ1}),1.0]])]});}
            var Q3;
            {var subQ0=sQuery(id+"F11.wireOp",EDGE,"E53");var subQ1=sQuery(id+"F11.wireOp",EDGE,"E52");var subQ2=makeQuery(id+"F11.imprint","INTERSECT",VERTEX,{"disambiguationData":[OD(0.0)],"derivedFrom":[subQ1,subQ0]});Q3=makeQuery(id+"F11.imprint","IMPRINT",FACE,{"disambiguationData":[TD([[makeQuery(id+"F11.imprint","IMPRINT",EDGE,{"disambiguationData":[TD([[subQ2,1.0]])],"derivedFrom":subQ1}),1.0]])]});}
            var Q4;
            {var subQ0=sQuery(id+"F11.wireOp",EDGE,"E53");var subQ1=sQuery(id+"F11.wireOp",EDGE,"E52");var subQ2=makeQuery(id+"F11.imprint","INTERSECT",VERTEX,{"disambiguationData":[OD(0.0)],"derivedFrom":[subQ1,subQ0]});Q4=makeQuery(id+"F11.imprint","IMPRINT",FACE,{"disambiguationData":[TD([[makeQuery(id+"F11.imprint","IMPRINT",EDGE,{"disambiguationData":[TD([[subQ2,1.0]])],"derivedFrom":subQ1}),-1.0]])]});}
            var Q5;
            Q5=makeQuery(id+"F11.imprint","IMPRINT",FACE,{"disambiguationData":[TD([[makeQuery(id+"F11.imprint","IMPRINT",EDGE,{"derivedFrom":sQuery(id+"F11.wireOp",EDGE,"E54")}),1.0]])]});
            var Q6;
            {var subQ0=sQuery(id+"F11.wireOp",EDGE,"E55");var subQ1=sQuery(id+"F11.wireOp",EDGE,"E41");var subQ2=makeQuery(id+"F11.imprint","INTERSECT",VERTEX,{"derivedFrom":[subQ1,subQ0]});Q6=makeQuery(id+"F11.imprint","IMPRINT",FACE,{"disambiguationData":[TD([[makeQuery(id+"F11.imprint","IMPRINT",EDGE,{"disambiguationData":[TD([[subQ2,-1.0]])],"derivedFrom":subQ1}),1.0]])]});}
            var Q7;
            {var subQ0=sQuery(id+"F11.wireOp",EDGE,"E55");var subQ1=sQuery(id+"F11.wireOp",EDGE,"E41");var subQ2=makeQuery(id+"F11.imprint","INTERSECT",VERTEX,{"derivedFrom":[subQ1,subQ0]});Q7=makeQuery(id+"F11.imprint","IMPRINT",FACE,{"disambiguationData":[TD([[makeQuery(id+"F11.imprint","IMPRINT",EDGE,{"disambiguationData":[TD([[subQ2,1.0]])],"derivedFrom":subQ1}),1.0]])]});}
            var Q8;
            {var subQ0=sQuery(id+"F11.wireOp",EDGE,"E41");var subQ1=makeQuery(id+"F11.imprint","INTERSECT",VERTEX,{"derivedFrom":[subQ0,sQuery(id+"F11.wireOp",EDGE,"E55")]});Q8=makeQuery(id+"F11.imprint","IMPRINT",FACE,{"disambiguationData":[TD([[makeQuery(id+"F11.imprint","IMPRINT",EDGE,{"disambiguationData":[TD([[subQ1,1.0]])],"derivedFrom":subQ0}),-1.0]])]});}
            var Q9;
            Q9=makeQuery(id+"F11.imprint","IMPRINT",FACE,{"disambiguationData":[TD([[makeQuery(id+"F11.imprint","IMPRINT",EDGE,{"derivedFrom":sQuery(id+"F11.wireOp",EDGE,"E51")}),1.0]])]});
            extrude(context, id + "F17", {"entities" : qUnion([Q0, Q1, Q2, Q3, Q4, Q5, Q6, Q7, Q8, Q9]), "operationType" : NewBodyOperationType.ADD, "depth" : 0.5 * mm, "offsetDistance" : 25 * mm});
        }
        {
            var Q0;
            {var subQ0=sQuery(id+"F12.wireOp",EDGE,"E72");var subQ1=sQuery(id+"F12.wireOp",EDGE,"E61");var subQ2=makeQuery(id+"F12.imprint","INTERSECT",VERTEX,{"derivedFrom":[subQ1,subQ0]});Q0=makeQuery(id+"F12.imprint","IMPRINT",FACE,{"disambiguationData":[TD([[makeQuery(id+"F12.imprint","IMPRINT",EDGE,{"disambiguationData":[TD([[subQ2,1.0]])],"derivedFrom":subQ1}),1.0]])]});}
            var Q1;
            {var subQ0=sQuery(id+"F12.wireOp",EDGE,"E72");var subQ1=sQuery(id+"F12.wireOp",EDGE,"E61");var subQ2=makeQuery(id+"F12.imprint","INTERSECT",VERTEX,{"derivedFrom":[subQ1,subQ0]});Q1=makeQuery(id+"F12.imprint","IMPRINT",FACE,{"disambiguationData":[TD([[makeQuery(id+"F12.imprint","IMPRINT",EDGE,{"disambiguationData":[TD([[subQ2,-1.0]])],"derivedFrom":subQ1}),1.0]])]});}
            var Q2;
            {var subQ0=sQuery(id+"F12.wireOp",EDGE,"E61");var subQ1=makeQuery(id+"F12.imprint","INTERSECT",VERTEX,{"derivedFrom":[subQ0,sQuery(id+"F12.wireOp",EDGE,"E72")]});Q2=makeQuery(id+"F12.imprint","IMPRINT",FACE,{"disambiguationData":[TD([[makeQuery(id+"F12.imprint","IMPRINT",EDGE,{"disambiguationData":[TD([[subQ1,1.0]])],"derivedFrom":subQ0}),-1.0]])]});}
            var Q3;
            {var subQ0=sQuery(id+"F12.wireOp",EDGE,"E73");var subQ1=sQuery(id+"F12.wireOp",EDGE,"E72");var subQ2=makeQuery(id+"F12.imprint","INTERSECT",VERTEX,{"disambiguationData":[OD(0.0)],"derivedFrom":[subQ1,subQ0]});Q3=makeQuery(id+"F12.imprint","IMPRINT",FACE,{"disambiguationData":[TD([[makeQuery(id+"F12.imprint","IMPRINT",EDGE,{"disambiguationData":[TD([[subQ2,-1.0]])],"derivedFrom":subQ1}),1.0]])]});}
            var Q4;
            {var subQ0=sQuery(id+"F12.wireOp",EDGE,"E73");var subQ1=sQuery(id+"F12.wireOp",EDGE,"E72");var subQ2=makeQuery(id+"F12.imprint","INTERSECT",VERTEX,{"disambiguationData":[OD(0.0)],"derivedFrom":[subQ1,subQ0]});Q4=makeQuery(id+"F12.imprint","IMPRINT",FACE,{"disambiguationData":[TD([[makeQuery(id+"F12.imprint","IMPRINT",EDGE,{"disambiguationData":[TD([[subQ2,-1.0]])],"derivedFrom":subQ1}),-1.0]])]});}
            var Q5;
            Q5=makeQuery(id+"F12.imprint","IMPRINT",FACE,{"disambiguationData":[TD([[makeQuery(id+"F12.imprint","IMPRINT",EDGE,{"derivedFrom":sQuery(id+"F12.wireOp",EDGE,"E74")}),1.0]])]});
            var Q6;
            Q6=makeQuery(id+"F12.imprint","IMPRINT",FACE,{"disambiguationData":[TD([[makeQuery(id+"F12.imprint","IMPRINT",EDGE,{"derivedFrom":sQuery(id+"F12.wireOp",EDGE,"E71")}),1.0]])]});
            var Q7;
            {var subQ0=sQuery(id+"F12.wireOp",EDGE,"E75");var subQ1=sQuery(id+"F12.wireOp",EDGE,"E61");var subQ2=makeQuery(id+"F12.imprint","INTERSECT",VERTEX,{"derivedFrom":[subQ1,subQ0]});Q7=makeQuery(id+"F12.imprint","IMPRINT",FACE,{"disambiguationData":[TD([[makeQuery(id+"F12.imprint","IMPRINT",EDGE,{"disambiguationData":[TD([[subQ2,-1.0]])],"derivedFrom":subQ1}),1.0]])]});}
            var Q8;
            {var subQ0=sQuery(id+"F12.wireOp",EDGE,"E75");var subQ1=sQuery(id+"F12.wireOp",EDGE,"E61");var subQ2=makeQuery(id+"F12.imprint","INTERSECT",VERTEX,{"derivedFrom":[subQ1,subQ0]});Q8=makeQuery(id+"F12.imprint","IMPRINT",FACE,{"disambiguationData":[TD([[makeQuery(id+"F12.imprint","IMPRINT",EDGE,{"disambiguationData":[TD([[subQ2,1.0]])],"derivedFrom":subQ1}),1.0]])]});}
            var Q9;
            {var subQ0=sQuery(id+"F12.wireOp",EDGE,"E61");var subQ1=makeQuery(id+"F12.imprint","INTERSECT",VERTEX,{"derivedFrom":[subQ0,sQuery(id+"F12.wireOp",EDGE,"E75")]});Q9=makeQuery(id+"F12.imprint","IMPRINT",FACE,{"disambiguationData":[TD([[makeQuery(id+"F12.imprint","IMPRINT",EDGE,{"disambiguationData":[TD([[subQ1,1.0]])],"derivedFrom":subQ0}),-1.0]])]});}
            var Q10;
            {var subQ0=sQuery(id+"F12.wireOp",EDGE,"E76");var subQ1=sQuery(id+"F12.wireOp",EDGE,"E75");var subQ2=makeQuery(id+"F12.imprint","INTERSECT",VERTEX,{"disambiguationData":[OD(0.0)],"derivedFrom":[subQ1,subQ0]});Q10=makeQuery(id+"F12.imprint","IMPRINT",FACE,{"disambiguationData":[TD([[makeQuery(id+"F12.imprint","IMPRINT",EDGE,{"disambiguationData":[TD([[subQ2,-1.0]])],"derivedFrom":subQ1}),-1.0]])]});}
            var Q11;
            {var subQ0=sQuery(id+"F12.wireOp",EDGE,"E76");var subQ1=sQuery(id+"F12.wireOp",EDGE,"E75");var subQ2=makeQuery(id+"F12.imprint","INTERSECT",VERTEX,{"disambiguationData":[OD(0.0)],"derivedFrom":[subQ1,subQ0]});Q11=makeQuery(id+"F12.imprint","IMPRINT",FACE,{"disambiguationData":[TD([[makeQuery(id+"F12.imprint","IMPRINT",EDGE,{"disambiguationData":[TD([[subQ2,-1.0]])],"derivedFrom":subQ1}),1.0]])]});}
            extrude(context, id + "F18", {"entities" : qUnion([Q0, Q1, Q2, Q3, Q4, Q5, Q6, Q7, Q8, Q9, Q10, Q11]), "operationType" : NewBodyOperationType.ADD, "depth" : 0.5 * mm, "offsetDistance" : 25 * mm});
        }
        {
            var Q0;
            {var subQ0=sQuery(id+"F13.wireOp",EDGE,"E81");var subQ1=makeQuery(id+"F13.imprint","INTERSECT",VERTEX,{"derivedFrom":[subQ0,sQuery(id+"F13.wireOp",EDGE,"E92")]});Q0=makeQuery(id+"F13.imprint","IMPRINT",FACE,{"disambiguationData":[TD([[makeQuery(id+"F13.imprint","IMPRINT",EDGE,{"disambiguationData":[TD([[subQ1,1.0]])],"derivedFrom":subQ0}),-1.0]])]});}
            var Q1;
            {var subQ0=sQuery(id+"F13.wireOp",EDGE,"E92");var subQ1=sQuery(id+"F13.wireOp",EDGE,"E81");var subQ2=makeQuery(id+"F13.imprint","INTERSECT",VERTEX,{"derivedFrom":[subQ1,subQ0]});Q1=makeQuery(id+"F13.imprint","IMPRINT",FACE,{"disambiguationData":[TD([[makeQuery(id+"F13.imprint","IMPRINT",EDGE,{"disambiguationData":[TD([[subQ2,1.0]])],"derivedFrom":subQ1}),1.0]])]});}
            var Q2;
            {var subQ0=sQuery(id+"F13.wireOp",EDGE,"E92");var subQ1=sQuery(id+"F13.wireOp",EDGE,"E81");var subQ2=makeQuery(id+"F13.imprint","INTERSECT",VERTEX,{"derivedFrom":[subQ1,subQ0]});Q2=makeQuery(id+"F13.imprint","IMPRINT",FACE,{"disambiguationData":[TD([[makeQuery(id+"F13.imprint","IMPRINT",EDGE,{"disambiguationData":[TD([[subQ2,-1.0]])],"derivedFrom":subQ1}),1.0]])]});}
            var Q3;
            {var subQ0=sQuery(id+"F13.wireOp",EDGE,"E93");var subQ1=sQuery(id+"F13.wireOp",EDGE,"E92");var subQ2=makeQuery(id+"F13.imprint","INTERSECT",VERTEX,{"disambiguationData":[OD(0.0)],"derivedFrom":[subQ1,subQ0]});Q3=makeQuery(id+"F13.imprint","IMPRINT",FACE,{"disambiguationData":[TD([[makeQuery(id+"F13.imprint","IMPRINT",EDGE,{"disambiguationData":[TD([[subQ2,-1.0]])],"derivedFrom":subQ1}),1.0]])]});}
            var Q4;
            {var subQ0=sQuery(id+"F13.wireOp",EDGE,"E93");var subQ1=sQuery(id+"F13.wireOp",EDGE,"E92");var subQ2=makeQuery(id+"F13.imprint","INTERSECT",VERTEX,{"disambiguationData":[OD(0.0)],"derivedFrom":[subQ1,subQ0]});Q4=makeQuery(id+"F13.imprint","IMPRINT",FACE,{"disambiguationData":[TD([[makeQuery(id+"F13.imprint","IMPRINT",EDGE,{"disambiguationData":[TD([[subQ2,-1.0]])],"derivedFrom":subQ1}),-1.0]])]});}
            var Q5;
            Q5=makeQuery(id+"F13.imprint","IMPRINT",FACE,{"disambiguationData":[TD([[makeQuery(id+"F13.imprint","IMPRINT",EDGE,{"derivedFrom":sQuery(id+"F13.wireOp",EDGE,"E94")}),1.0]])]});
            var Q6;
            Q6=makeQuery(id+"F13.imprint","IMPRINT",FACE,{"disambiguationData":[TD([[makeQuery(id+"F13.imprint","IMPRINT",EDGE,{"derivedFrom":sQuery(id+"F13.wireOp",EDGE,"E91")}),1.0]])]});
            var Q7;
            {var subQ0=sQuery(id+"F13.wireOp",EDGE,"E95");var subQ1=sQuery(id+"F13.wireOp",EDGE,"E81");var subQ2=makeQuery(id+"F13.imprint","INTERSECT",VERTEX,{"derivedFrom":[subQ1,subQ0]});Q7=makeQuery(id+"F13.imprint","IMPRINT",FACE,{"disambiguationData":[TD([[makeQuery(id+"F13.imprint","IMPRINT",EDGE,{"disambiguationData":[TD([[subQ2,1.0]])],"derivedFrom":subQ1}),1.0]])]});}
            var Q8;
            {var subQ0=sQuery(id+"F13.wireOp",EDGE,"E95");var subQ1=sQuery(id+"F13.wireOp",EDGE,"E81");var subQ2=makeQuery(id+"F13.imprint","INTERSECT",VERTEX,{"derivedFrom":[subQ1,subQ0]});Q8=makeQuery(id+"F13.imprint","IMPRINT",FACE,{"disambiguationData":[TD([[makeQuery(id+"F13.imprint","IMPRINT",EDGE,{"disambiguationData":[TD([[subQ2,-1.0]])],"derivedFrom":subQ1}),1.0]])]});}
            var Q9;
            {var subQ0=sQuery(id+"F13.wireOp",EDGE,"E81");var subQ1=makeQuery(id+"F13.imprint","INTERSECT",VERTEX,{"derivedFrom":[subQ0,sQuery(id+"F13.wireOp",EDGE,"E95")]});Q9=makeQuery(id+"F13.imprint","IMPRINT",FACE,{"disambiguationData":[TD([[makeQuery(id+"F13.imprint","IMPRINT",EDGE,{"disambiguationData":[TD([[subQ1,1.0]])],"derivedFrom":subQ0}),-1.0]])]});}
            var Q10;
            {var subQ0=sQuery(id+"F13.wireOp",EDGE,"E98");var subQ1=sQuery(id+"F13.wireOp",EDGE,"E81");var subQ2=makeQuery(id+"F13.imprint","INTERSECT",VERTEX,{"derivedFrom":[subQ1,subQ0]});Q10=makeQuery(id+"F13.imprint","IMPRINT",FACE,{"disambiguationData":[TD([[makeQuery(id+"F13.imprint","IMPRINT",EDGE,{"disambiguationData":[TD([[subQ2,-1.0]])],"derivedFrom":subQ1}),-1.0]])]});}
            var Q11;
            {var subQ0=sQuery(id+"F13.wireOp",EDGE,"E98");var subQ1=sQuery(id+"F13.wireOp",EDGE,"E81");var subQ2=makeQuery(id+"F13.imprint","INTERSECT",VERTEX,{"derivedFrom":[subQ1,subQ0]});Q11=makeQuery(id+"F13.imprint","IMPRINT",FACE,{"disambiguationData":[TD([[makeQuery(id+"F13.imprint","IMPRINT",EDGE,{"disambiguationData":[TD([[subQ2,-1.0]])],"derivedFrom":subQ1}),1.0]])]});}
            extrude(context, id + "F19", {"entities" : qUnion([Q0, Q1, Q2, Q3, Q4, Q5, Q6, Q7, Q8, Q9, Q10, Q11]), "operationType" : NewBodyOperationType.ADD, "depth" : 0.5 * mm, "offsetDistance" : 25 * mm});
        }
        {
            var Q0;
            {var subQ0=sQuery(id+"F14.wireOp",EDGE,"E112");var subQ1=sQuery(id+"F14.wireOp",EDGE,"E101");var subQ2=makeQuery(id+"F14.imprint","INTERSECT",VERTEX,{"derivedFrom":[subQ1,subQ0]});Q0=makeQuery(id+"F14.imprint","IMPRINT",FACE,{"disambiguationData":[TD([[makeQuery(id+"F14.imprint","IMPRINT",EDGE,{"disambiguationData":[TD([[subQ2,1.0]])],"derivedFrom":subQ1}),1.0]])]});}
            var Q1;
            {var subQ0=sQuery(id+"F14.wireOp",EDGE,"E101");var subQ1=makeQuery(id+"F14.imprint","INTERSECT",VERTEX,{"derivedFrom":[subQ0,sQuery(id+"F14.wireOp",EDGE,"E112")]});Q1=makeQuery(id+"F14.imprint","IMPRINT",FACE,{"disambiguationData":[TD([[makeQuery(id+"F14.imprint","IMPRINT",EDGE,{"disambiguationData":[TD([[subQ1,1.0]])],"derivedFrom":subQ0}),-1.0]])]});}
            var Q2;
            {var subQ0=sQuery(id+"F14.wireOp",EDGE,"E112");var subQ1=sQuery(id+"F14.wireOp",EDGE,"E101");var subQ2=makeQuery(id+"F14.imprint","INTERSECT",VERTEX,{"derivedFrom":[subQ1,subQ0]});Q2=makeQuery(id+"F14.imprint","IMPRINT",FACE,{"disambiguationData":[TD([[makeQuery(id+"F14.imprint","IMPRINT",EDGE,{"disambiguationData":[TD([[subQ2,-1.0]])],"derivedFrom":subQ1}),1.0]])]});}
            var Q3;
            {var subQ0=sQuery(id+"F14.wireOp",EDGE,"E113");var subQ1=sQuery(id+"F14.wireOp",EDGE,"E112");var subQ2=makeQuery(id+"F14.imprint","INTERSECT",VERTEX,{"disambiguationData":[OD(0.0)],"derivedFrom":[subQ1,subQ0]});Q3=makeQuery(id+"F14.imprint","IMPRINT",FACE,{"disambiguationData":[TD([[makeQuery(id+"F14.imprint","IMPRINT",EDGE,{"disambiguationData":[TD([[subQ2,-1.0]])],"derivedFrom":subQ1}),1.0]])]});}
            var Q4;
            {var subQ0=sQuery(id+"F14.wireOp",EDGE,"E113");var subQ1=sQuery(id+"F14.wireOp",EDGE,"E112");var subQ2=makeQuery(id+"F14.imprint","INTERSECT",VERTEX,{"disambiguationData":[OD(0.0)],"derivedFrom":[subQ1,subQ0]});Q4=makeQuery(id+"F14.imprint","IMPRINT",FACE,{"disambiguationData":[TD([[makeQuery(id+"F14.imprint","IMPRINT",EDGE,{"disambiguationData":[TD([[subQ2,-1.0]])],"derivedFrom":subQ1}),-1.0]])]});}
            var Q5;
            Q5=makeQuery(id+"F14.imprint","IMPRINT",FACE,{"disambiguationData":[TD([[makeQuery(id+"F14.imprint","IMPRINT",EDGE,{"derivedFrom":sQuery(id+"F14.wireOp",EDGE,"E114")}),1.0]])]});
            var Q6;
            Q6=makeQuery(id+"F14.imprint","IMPRINT",FACE,{"disambiguationData":[TD([[makeQuery(id+"F14.imprint","IMPRINT",EDGE,{"derivedFrom":sQuery(id+"F14.wireOp",EDGE,"E111")}),1.0]])]});
            var Q7;
            {var subQ0=sQuery(id+"F14.wireOp",EDGE,"E101");var subQ1=makeQuery(id+"F14.imprint","INTERSECT",VERTEX,{"derivedFrom":[subQ0,sQuery(id+"F14.wireOp",EDGE,"E115")]});Q7=makeQuery(id+"F14.imprint","IMPRINT",FACE,{"disambiguationData":[TD([[makeQuery(id+"F14.imprint","IMPRINT",EDGE,{"disambiguationData":[TD([[subQ1,1.0]])],"derivedFrom":subQ0}),-1.0]])]});}
            var Q8;
            {var subQ0=sQuery(id+"F14.wireOp",EDGE,"E115");var subQ1=sQuery(id+"F14.wireOp",EDGE,"E101");var subQ2=makeQuery(id+"F14.imprint","INTERSECT",VERTEX,{"derivedFrom":[subQ1,subQ0]});Q8=makeQuery(id+"F14.imprint","IMPRINT",FACE,{"disambiguationData":[TD([[makeQuery(id+"F14.imprint","IMPRINT",EDGE,{"disambiguationData":[TD([[subQ2,1.0]])],"derivedFrom":subQ1}),1.0]])]});}
            var Q9;
            {var subQ0=sQuery(id+"F14.wireOp",EDGE,"E115");var subQ1=sQuery(id+"F14.wireOp",EDGE,"E101");var subQ2=makeQuery(id+"F14.imprint","INTERSECT",VERTEX,{"derivedFrom":[subQ1,subQ0]});Q9=makeQuery(id+"F14.imprint","IMPRINT",FACE,{"disambiguationData":[TD([[makeQuery(id+"F14.imprint","IMPRINT",EDGE,{"disambiguationData":[TD([[subQ2,-1.0]])],"derivedFrom":subQ1}),1.0]])]});}
            var Q10;
            {var subQ0=sQuery(id+"F14.wireOp",EDGE,"E118");var subQ1=sQuery(id+"F14.wireOp",EDGE,"E101");var subQ2=makeQuery(id+"F14.imprint","INTERSECT",VERTEX,{"derivedFrom":[subQ1,subQ0]});Q10=makeQuery(id+"F14.imprint","IMPRINT",FACE,{"disambiguationData":[TD([[makeQuery(id+"F14.imprint","IMPRINT",EDGE,{"disambiguationData":[TD([[subQ2,-1.0]])],"derivedFrom":subQ1}),-1.0]])]});}
            var Q11;
            {var subQ0=sQuery(id+"F14.wireOp",EDGE,"E118");var subQ1=sQuery(id+"F14.wireOp",EDGE,"E101");var subQ2=makeQuery(id+"F14.imprint","INTERSECT",VERTEX,{"derivedFrom":[subQ1,subQ0]});Q11=makeQuery(id+"F14.imprint","IMPRINT",FACE,{"disambiguationData":[TD([[makeQuery(id+"F14.imprint","IMPRINT",EDGE,{"disambiguationData":[TD([[subQ2,-1.0]])],"derivedFrom":subQ1}),1.0]])]});}
            var Q12;
            {var subQ0=sQuery(id+"F14.wireOp",EDGE,"E119");var subQ1=sQuery(id+"F14.wireOp",EDGE,"E118");var subQ2=makeQuery(id+"F14.imprint","INTERSECT",VERTEX,{"disambiguationData":[OD(0.0)],"derivedFrom":[subQ1,subQ0]});Q12=makeQuery(id+"F14.imprint","IMPRINT",FACE,{"disambiguationData":[TD([[makeQuery(id+"F14.imprint","IMPRINT",EDGE,{"disambiguationData":[TD([[subQ2,-1.0]])],"derivedFrom":subQ1}),1.0]])]});}
            var Q13;
            {var subQ0=sQuery(id+"F14.wireOp",EDGE,"E119");var subQ1=sQuery(id+"F14.wireOp",EDGE,"E118");var subQ2=makeQuery(id+"F14.imprint","INTERSECT",VERTEX,{"disambiguationData":[OD(0.0)],"derivedFrom":[subQ1,subQ0]});Q13=makeQuery(id+"F14.imprint","IMPRINT",FACE,{"disambiguationData":[TD([[makeQuery(id+"F14.imprint","IMPRINT",EDGE,{"disambiguationData":[TD([[subQ2,-1.0]])],"derivedFrom":subQ1}),-1.0]])]});}
            extrude(context, id + "F20", {"entities" : qUnion([Q0, Q1, Q2, Q3, Q4, Q5, Q6, Q7, Q8, Q9, Q10, Q11, Q12, Q13]), "operationType" : NewBodyOperationType.ADD, "depth" : 0.5 * mm, "offsetDistance" : 25 * mm});
        }
        {
            var Q0;
            {var subQ0=sQuery(id+"F15.wireOp",EDGE,"E121");var subQ1=makeQuery(id+"F15.imprint","INTERSECT",VERTEX,{"derivedFrom":[subQ0,sQuery(id+"F15.wireOp",EDGE,"E132")]});Q0=makeQuery(id+"F15.imprint","IMPRINT",FACE,{"disambiguationData":[TD([[makeQuery(id+"F15.imprint","IMPRINT",EDGE,{"disambiguationData":[TD([[subQ1,1.0]])],"derivedFrom":subQ0}),-1.0]])]});}
            var Q1;
            {var subQ0=sQuery(id+"F15.wireOp",EDGE,"E132");var subQ1=sQuery(id+"F15.wireOp",EDGE,"E121");var subQ2=makeQuery(id+"F15.imprint","INTERSECT",VERTEX,{"derivedFrom":[subQ1,subQ0]});Q1=makeQuery(id+"F15.imprint","IMPRINT",FACE,{"disambiguationData":[TD([[makeQuery(id+"F15.imprint","IMPRINT",EDGE,{"disambiguationData":[TD([[subQ2,1.0]])],"derivedFrom":subQ1}),1.0]])]});}
            var Q2;
            {var subQ0=sQuery(id+"F15.wireOp",EDGE,"E132");var subQ1=sQuery(id+"F15.wireOp",EDGE,"E121");var subQ2=makeQuery(id+"F15.imprint","INTERSECT",VERTEX,{"derivedFrom":[subQ1,subQ0]});Q2=makeQuery(id+"F15.imprint","IMPRINT",FACE,{"disambiguationData":[TD([[makeQuery(id+"F15.imprint","IMPRINT",EDGE,{"disambiguationData":[TD([[subQ2,-1.0]])],"derivedFrom":subQ1}),1.0]])]});}
            var Q3;
            {var subQ0=sQuery(id+"F15.wireOp",EDGE,"E133");var subQ1=sQuery(id+"F15.wireOp",EDGE,"E132");var subQ2=makeQuery(id+"F15.imprint","INTERSECT",VERTEX,{"disambiguationData":[OD(0.0)],"derivedFrom":[subQ1,subQ0]});Q3=makeQuery(id+"F15.imprint","IMPRINT",FACE,{"disambiguationData":[TD([[makeQuery(id+"F15.imprint","IMPRINT",EDGE,{"disambiguationData":[TD([[subQ2,-1.0]])],"derivedFrom":subQ1}),1.0]])]});}
            var Q4;
            {var subQ0=sQuery(id+"F15.wireOp",EDGE,"E133");var subQ1=sQuery(id+"F15.wireOp",EDGE,"E132");var subQ2=makeQuery(id+"F15.imprint","INTERSECT",VERTEX,{"disambiguationData":[OD(0.0)],"derivedFrom":[subQ1,subQ0]});Q4=makeQuery(id+"F15.imprint","IMPRINT",FACE,{"disambiguationData":[TD([[makeQuery(id+"F15.imprint","IMPRINT",EDGE,{"disambiguationData":[TD([[subQ2,-1.0]])],"derivedFrom":subQ1}),-1.0]])]});}
            var Q5;
            Q5=makeQuery(id+"F15.imprint","IMPRINT",FACE,{"disambiguationData":[TD([[makeQuery(id+"F15.imprint","IMPRINT",EDGE,{"derivedFrom":sQuery(id+"F15.wireOp",EDGE,"E134")}),1.0]])]});
            var Q6;
            Q6=makeQuery(id+"F15.imprint","IMPRINT",FACE,{"disambiguationData":[TD([[makeQuery(id+"F15.imprint","IMPRINT",EDGE,{"derivedFrom":sQuery(id+"F15.wireOp",EDGE,"E131")}),1.0]])]});
            var Q7;
            {var subQ0=sQuery(id+"F15.wireOp",EDGE,"E121");var subQ1=makeQuery(id+"F15.imprint","INTERSECT",VERTEX,{"derivedFrom":[subQ0,sQuery(id+"F15.wireOp",EDGE,"E135")]});Q7=makeQuery(id+"F15.imprint","IMPRINT",FACE,{"disambiguationData":[TD([[makeQuery(id+"F15.imprint","IMPRINT",EDGE,{"disambiguationData":[TD([[subQ1,1.0]])],"derivedFrom":subQ0}),-1.0]])]});}
            var Q8;
            {var subQ0=sQuery(id+"F15.wireOp",EDGE,"E135");var subQ1=sQuery(id+"F15.wireOp",EDGE,"E121");var subQ2=makeQuery(id+"F15.imprint","INTERSECT",VERTEX,{"derivedFrom":[subQ1,subQ0]});Q8=makeQuery(id+"F15.imprint","IMPRINT",FACE,{"disambiguationData":[TD([[makeQuery(id+"F15.imprint","IMPRINT",EDGE,{"disambiguationData":[TD([[subQ2,1.0]])],"derivedFrom":subQ1}),1.0]])]});}
            var Q9;
            {var subQ0=sQuery(id+"F15.wireOp",EDGE,"E135");var subQ1=sQuery(id+"F15.wireOp",EDGE,"E121");var subQ2=makeQuery(id+"F15.imprint","INTERSECT",VERTEX,{"derivedFrom":[subQ1,subQ0]});Q9=makeQuery(id+"F15.imprint","IMPRINT",FACE,{"disambiguationData":[TD([[makeQuery(id+"F15.imprint","IMPRINT",EDGE,{"disambiguationData":[TD([[subQ2,-1.0]])],"derivedFrom":subQ1}),1.0]])]});}
            var Q10;
            {var subQ0=sQuery(id+"F15.wireOp",EDGE,"E139");var subQ1=sQuery(id+"F15.wireOp",EDGE,"E138");var subQ2=makeQuery(id+"F15.imprint","INTERSECT",VERTEX,{"disambiguationData":[OD(0.0)],"derivedFrom":[subQ1,subQ0]});Q10=makeQuery(id+"F15.imprint","IMPRINT",FACE,{"disambiguationData":[TD([[makeQuery(id+"F15.imprint","IMPRINT",EDGE,{"disambiguationData":[TD([[subQ2,-1.0]])],"derivedFrom":subQ1}),1.0]])]});}
            var Q11;
            {var subQ0=sQuery(id+"F15.wireOp",EDGE,"E139");var subQ1=sQuery(id+"F15.wireOp",EDGE,"E138");var subQ2=makeQuery(id+"F15.imprint","INTERSECT",VERTEX,{"disambiguationData":[OD(0.0)],"derivedFrom":[subQ1,subQ0]});Q11=makeQuery(id+"F15.imprint","IMPRINT",FACE,{"disambiguationData":[TD([[makeQuery(id+"F15.imprint","IMPRINT",EDGE,{"disambiguationData":[TD([[subQ2,-1.0]])],"derivedFrom":subQ1}),-1.0]])]});}
            extrude(context, id + "F21", {"entities" : qUnion([Q0, Q1, Q2, Q3, Q4, Q5, Q6, Q7, Q8, Q9, Q10, Q11]), "operationType" : NewBodyOperationType.ADD, "depth" : 0.5 * mm, "offsetDistance" : 25 * mm});
        }
        {
            var Q0;
            {var subQ0=sQuery(id+"F16.wireOp",EDGE,"E141");var subQ1=makeQuery(id+"F16.imprint","INTERSECT",VERTEX,{"derivedFrom":[subQ0,sQuery(id+"F16.wireOp",EDGE,"E152")]});Q0=makeQuery(id+"F16.imprint","IMPRINT",FACE,{"disambiguationData":[TD([[makeQuery(id+"F16.imprint","IMPRINT",EDGE,{"disambiguationData":[TD([[subQ1,1.0]])],"derivedFrom":subQ0}),-1.0]])]});}
            var Q1;
            {var subQ0=sQuery(id+"F16.wireOp",EDGE,"E152");var subQ1=sQuery(id+"F16.wireOp",EDGE,"E141");var subQ2=makeQuery(id+"F16.imprint","INTERSECT",VERTEX,{"derivedFrom":[subQ1,subQ0]});Q1=makeQuery(id+"F16.imprint","IMPRINT",FACE,{"disambiguationData":[TD([[makeQuery(id+"F16.imprint","IMPRINT",EDGE,{"disambiguationData":[TD([[subQ2,1.0]])],"derivedFrom":subQ1}),1.0]])]});}
            var Q2;
            {var subQ0=sQuery(id+"F16.wireOp",EDGE,"E152");var subQ1=sQuery(id+"F16.wireOp",EDGE,"E141");var subQ2=makeQuery(id+"F16.imprint","INTERSECT",VERTEX,{"derivedFrom":[subQ1,subQ0]});Q2=makeQuery(id+"F16.imprint","IMPRINT",FACE,{"disambiguationData":[TD([[makeQuery(id+"F16.imprint","IMPRINT",EDGE,{"disambiguationData":[TD([[subQ2,-1.0]])],"derivedFrom":subQ1}),1.0]])]});}
            var Q3;
            {var subQ0=sQuery(id+"F16.wireOp",EDGE,"E153");var subQ1=sQuery(id+"F16.wireOp",EDGE,"E152");var subQ2=makeQuery(id+"F16.imprint","INTERSECT",VERTEX,{"disambiguationData":[OD(0.0)],"derivedFrom":[subQ1,subQ0]});Q3=makeQuery(id+"F16.imprint","IMPRINT",FACE,{"disambiguationData":[TD([[makeQuery(id+"F16.imprint","IMPRINT",EDGE,{"disambiguationData":[TD([[subQ2,1.0]])],"derivedFrom":subQ1}),1.0]])]});}
            var Q4;
            {var subQ0=sQuery(id+"F16.wireOp",EDGE,"E153");var subQ1=sQuery(id+"F16.wireOp",EDGE,"E152");var subQ2=makeQuery(id+"F16.imprint","INTERSECT",VERTEX,{"disambiguationData":[OD(0.0)],"derivedFrom":[subQ1,subQ0]});Q4=makeQuery(id+"F16.imprint","IMPRINT",FACE,{"disambiguationData":[TD([[makeQuery(id+"F16.imprint","IMPRINT",EDGE,{"disambiguationData":[TD([[subQ2,1.0]])],"derivedFrom":subQ1}),-1.0]])]});}
            var Q5;
            Q5=makeQuery(id+"F16.imprint","IMPRINT",FACE,{"disambiguationData":[TD([[makeQuery(id+"F16.imprint","IMPRINT",EDGE,{"derivedFrom":sQuery(id+"F16.wireOp",EDGE,"E154")}),1.0]])]});
            var Q6;
            Q6=makeQuery(id+"F16.imprint","IMPRINT",FACE,{"disambiguationData":[TD([[makeQuery(id+"F16.imprint","IMPRINT",EDGE,{"derivedFrom":sQuery(id+"F16.wireOp",EDGE,"E151")}),1.0]])]});
            var Q7;
            {var subQ0=sQuery(id+"F16.wireOp",EDGE,"E141");var subQ1=makeQuery(id+"F16.imprint","INTERSECT",VERTEX,{"derivedFrom":[subQ0,sQuery(id+"F16.wireOp",EDGE,"E155")]});Q7=makeQuery(id+"F16.imprint","IMPRINT",FACE,{"disambiguationData":[TD([[makeQuery(id+"F16.imprint","IMPRINT",EDGE,{"disambiguationData":[TD([[subQ1,1.0]])],"derivedFrom":subQ0}),-1.0]])]});}
            var Q8;
            {var subQ0=sQuery(id+"F16.wireOp",EDGE,"E155");var subQ1=sQuery(id+"F16.wireOp",EDGE,"E141");var subQ2=makeQuery(id+"F16.imprint","INTERSECT",VERTEX,{"derivedFrom":[subQ1,subQ0]});Q8=makeQuery(id+"F16.imprint","IMPRINT",FACE,{"disambiguationData":[TD([[makeQuery(id+"F16.imprint","IMPRINT",EDGE,{"disambiguationData":[TD([[subQ2,1.0]])],"derivedFrom":subQ1}),1.0]])]});}
            var Q9;
            {var subQ0=sQuery(id+"F16.wireOp",EDGE,"E155");var subQ1=sQuery(id+"F16.wireOp",EDGE,"E141");var subQ2=makeQuery(id+"F16.imprint","INTERSECT",VERTEX,{"derivedFrom":[subQ1,subQ0]});Q9=makeQuery(id+"F16.imprint","IMPRINT",FACE,{"disambiguationData":[TD([[makeQuery(id+"F16.imprint","IMPRINT",EDGE,{"disambiguationData":[TD([[subQ2,-1.0]])],"derivedFrom":subQ1}),1.0]])]});}
            var Q10;
            {var subQ0=sQuery(id+"F16.wireOp",EDGE,"E156");var subQ1=sQuery(id+"F16.wireOp",EDGE,"E155");var subQ2=makeQuery(id+"F16.imprint","INTERSECT",VERTEX,{"disambiguationData":[OD(0.0)],"derivedFrom":[subQ1,subQ0]});Q10=makeQuery(id+"F16.imprint","IMPRINT",FACE,{"disambiguationData":[TD([[makeQuery(id+"F16.imprint","IMPRINT",EDGE,{"disambiguationData":[TD([[subQ2,1.0]])],"derivedFrom":subQ1}),1.0]])]});}
            var Q11;
            {var subQ0=sQuery(id+"F16.wireOp",EDGE,"E156");var subQ1=sQuery(id+"F16.wireOp",EDGE,"E155");var subQ2=makeQuery(id+"F16.imprint","INTERSECT",VERTEX,{"disambiguationData":[OD(0.0)],"derivedFrom":[subQ1,subQ0]});Q11=makeQuery(id+"F16.imprint","IMPRINT",FACE,{"disambiguationData":[TD([[makeQuery(id+"F16.imprint","IMPRINT",EDGE,{"disambiguationData":[TD([[subQ2,1.0]])],"derivedFrom":subQ1}),-1.0]])]});}
            var Q12;
            {var subQ0=sQuery(id+"F16.wireOp",EDGE,"E158");var subQ1=sQuery(id+"F16.wireOp",EDGE,"E141");var subQ2=makeQuery(id+"F16.imprint","INTERSECT",VERTEX,{"derivedFrom":[subQ1,subQ0]});Q12=makeQuery(id+"F16.imprint","IMPRINT",FACE,{"disambiguationData":[TD([[makeQuery(id+"F16.imprint","IMPRINT",EDGE,{"disambiguationData":[TD([[subQ2,-1.0]])],"derivedFrom":subQ1}),1.0]])]});}
            var Q13;
            {var subQ0=sQuery(id+"F16.wireOp",EDGE,"E158");var subQ1=sQuery(id+"F16.wireOp",EDGE,"E141");var subQ2=makeQuery(id+"F16.imprint","INTERSECT",VERTEX,{"derivedFrom":[subQ1,subQ0]});Q13=makeQuery(id+"F16.imprint","IMPRINT",FACE,{"disambiguationData":[TD([[makeQuery(id+"F16.imprint","IMPRINT",EDGE,{"disambiguationData":[TD([[subQ2,-1.0]])],"derivedFrom":subQ1}),-1.0]])]});}
            extrude(context, id + "F22", {"entities" : qUnion([Q0, Q1, Q2, Q3, Q4, Q5, Q6, Q7, Q8, Q9, Q10, Q11, Q12, Q13]), "operationType" : NewBodyOperationType.ADD, "depth" : 0.5 * mm, "offsetDistance" : 25 * mm});
        }
        {
            var Q0;
            Q0=makeQuery(id+"F17.opExtrude","CAP_EDGE",EDGE,{"disambiguationData":[OSD([sQuery(id+"F11.wireOp",EDGE,"E47")])],"isStart":false});
            var Q1;
            Q1=makeQuery(id+"F17.opExtrude","CAP_EDGE",EDGE,{"disambiguationData":[OSD([sQuery(id+"F11.wireOp",EDGE,"E45")])],"isStart":false});
            var Q2;
            Q2=makeQuery(id+"F17.opExtrude","CAP_EDGE",EDGE,{"disambiguationData":[OSD([sQuery(id+"F11.wireOp",EDGE,"E53")])],"isStart":false});
            var Q3;
            Q3=makeQuery(id+"F17.opExtrude","CAP_EDGE",EDGE,{"disambiguationData":[OSD([sQuery(id+"F11.wireOp",EDGE,"E54")])],"isStart":false});
            var Q4;
            Q4=makeQuery(id+"F17.opExtrude","CAP_EDGE",EDGE,{"disambiguationData":[OSD([sQuery(id+"F11.wireOp",EDGE,"E51")])],"isStart":false});
            fillet(context, id + "F23", {"entities" : qUnion([Q0, Q1, Q2, Q3, Q4]), "radius" : 0.5 * mm, "tangentPropagation" : true, "allowEdgeOverflow" : false});
        }
        {
            var Q0;
            Q0=makeQuery(id+"F18.opExtrude","CAP_EDGE",EDGE,{"disambiguationData":[OSD([sQuery(id+"F12.wireOp",EDGE,"E67")])],"isStart":false});
            var Q1;
            Q1=makeQuery(id+"F18.opExtrude","CAP_EDGE",EDGE,{"disambiguationData":[OSD([sQuery(id+"F12.wireOp",EDGE,"E76")])],"isStart":false});
            var Q2;
            Q2=makeQuery(id+"F18.opExtrude","CAP_EDGE",EDGE,{"disambiguationData":[OSD([sQuery(id+"F12.wireOp",EDGE,"E65")])],"isStart":false});
            var Q3;
            Q3=makeQuery(id+"F18.opExtrude","CAP_EDGE",EDGE,{"disambiguationData":[OSD([sQuery(id+"F12.wireOp",EDGE,"E73")])],"isStart":false});
            var Q4;
            Q4=makeQuery(id+"F18.opExtrude","CAP_EDGE",EDGE,{"disambiguationData":[OSD([sQuery(id+"F12.wireOp",EDGE,"E74")])],"isStart":false});
            var Q5;
            Q5=makeQuery(id+"F18.opExtrude","CAP_EDGE",EDGE,{"disambiguationData":[OSD([sQuery(id+"F12.wireOp",EDGE,"E71")])],"isStart":false});
            fillet(context, id + "F24", {"entities" : qUnion([Q0, Q1, Q2, Q3, Q4, Q5]), "radius" : 0.5 * mm, "tangentPropagation" : true, "allowEdgeOverflow" : false});
        }
        {
            var Q0;
            Q0=makeQuery(id+"F19.opExtrude","CAP_EDGE",EDGE,{"disambiguationData":[OSD([sQuery(id+"F13.wireOp",EDGE,"E88")])],"isStart":false});
            var Q1;
            Q1=makeQuery(id+"F19.opExtrude","CAP_EDGE",EDGE,{"disambiguationData":[OSD([sQuery(id+"F13.wireOp",EDGE,"E87")])],"isStart":false});
            var Q2;
            Q2=makeQuery(id+"F19.opExtrude","CAP_EDGE",EDGE,{"disambiguationData":[OSD([sQuery(id+"F13.wireOp",EDGE,"E85")])],"isStart":false});
            var Q3;
            Q3=makeQuery(id+"F19.opExtrude","CAP_EDGE",EDGE,{"disambiguationData":[OSD([sQuery(id+"F13.wireOp",EDGE,"E93")])],"isStart":false});
            var Q4;
            Q4=makeQuery(id+"F19.opExtrude","CAP_EDGE",EDGE,{"disambiguationData":[OSD([sQuery(id+"F13.wireOp",EDGE,"E94")])],"isStart":false});
            var Q5;
            Q5=makeQuery(id+"F19.opExtrude","CAP_EDGE",EDGE,{"disambiguationData":[OSD([sQuery(id+"F13.wireOp",EDGE,"E91")])],"isStart":false});
            fillet(context, id + "F25", {"entities" : qUnion([Q0, Q1, Q2, Q3, Q4, Q5]), "radius" : 0.5 * mm, "tangentPropagation" : true, "allowEdgeOverflow" : false});
        }
        {
            var Q0;
            Q0=makeQuery(id+"F20.opExtrude","CAP_EDGE",EDGE,{"disambiguationData":[OSD([sQuery(id+"F14.wireOp",EDGE,"E108")])],"isStart":false});
            var Q1;
            Q1=makeQuery(id+"F20.opExtrude","CAP_EDGE",EDGE,{"disambiguationData":[OSD([sQuery(id+"F14.wireOp",EDGE,"E119")])],"isStart":false});
            var Q2;
            Q2=makeQuery(id+"F20.opExtrude","CAP_EDGE",EDGE,{"disambiguationData":[OSD([sQuery(id+"F14.wireOp",EDGE,"E107")])],"isStart":false});
            var Q3;
            Q3=makeQuery(id+"F20.opExtrude","CAP_EDGE",EDGE,{"disambiguationData":[OSD([sQuery(id+"F14.wireOp",EDGE,"E105")])],"isStart":false});
            var Q4;
            Q4=makeQuery(id+"F20.opExtrude","CAP_EDGE",EDGE,{"disambiguationData":[OSD([sQuery(id+"F14.wireOp",EDGE,"E113")])],"isStart":false});
            var Q5;
            Q5=makeQuery(id+"F20.opExtrude","CAP_EDGE",EDGE,{"disambiguationData":[OSD([sQuery(id+"F14.wireOp",EDGE,"E114")])],"isStart":false});
            var Q6;
            Q6=makeQuery(id+"F20.opExtrude","CAP_EDGE",EDGE,{"disambiguationData":[OSD([sQuery(id+"F14.wireOp",EDGE,"E111")])],"isStart":false});
            fillet(context, id + "F26", {"entities" : qUnion([Q0, Q1, Q2, Q3, Q4, Q5, Q6]), "radius" : 0.5 * mm, "tangentPropagation" : true, "allowEdgeOverflow" : false});
        }
        {
            var Q0;
            Q0=makeQuery(id+"F21.opExtrude","CAP_EDGE",EDGE,{"disambiguationData":[OSD([sQuery(id+"F15.wireOp",EDGE,"E125")])],"isStart":false});
            var Q1;
            Q1=makeQuery(id+"F21.opExtrude","CAP_EDGE",EDGE,{"disambiguationData":[OSD([sQuery(id+"F15.wireOp",EDGE,"E133")])],"isStart":false});
            var Q2;
            Q2=makeQuery(id+"F21.opExtrude","CAP_EDGE",EDGE,{"disambiguationData":[OSD([sQuery(id+"F15.wireOp",EDGE,"E134")])],"isStart":false});
            var Q3;
            Q3=makeQuery(id+"F21.opExtrude","CAP_EDGE",EDGE,{"disambiguationData":[OSD([sQuery(id+"F15.wireOp",EDGE,"E131")])],"isStart":false});
            var Q4;
            Q4=makeQuery(id+"F21.opExtrude","CAP_EDGE",EDGE,{"disambiguationData":[OSD([sQuery(id+"F15.wireOp",EDGE,"E127")])],"isStart":false});
            var Q5;
            Q5=makeQuery(id+"F21.opExtrude","CAP_EDGE",EDGE,{"disambiguationData":[OSD([sQuery(id+"F15.wireOp",EDGE,"E139")])],"isStart":false});
            fillet(context, id + "F27", {"entities" : qUnion([Q0, Q1, Q2, Q3, Q4, Q5]), "radius" : 0.5 * mm, "tangentPropagation" : true, "allowEdgeOverflow" : false});
        }
        {
            var Q0;
            Q0=makeQuery(id+"F22.opExtrude","CAP_EDGE",EDGE,{"disambiguationData":[OSD([sQuery(id+"F16.wireOp",EDGE,"E148")])],"isStart":false});
            var Q1;
            Q1=makeQuery(id+"F22.opExtrude","CAP_EDGE",EDGE,{"disambiguationData":[OSD([sQuery(id+"F16.wireOp",EDGE,"E147")])],"isStart":false});
            var Q2;
            Q2=makeQuery(id+"F22.opExtrude","CAP_EDGE",EDGE,{"disambiguationData":[OSD([sQuery(id+"F16.wireOp",EDGE,"E156")])],"isStart":false});
            var Q3;
            Q3=makeQuery(id+"F22.opExtrude","CAP_EDGE",EDGE,{"disambiguationData":[OSD([sQuery(id+"F16.wireOp",EDGE,"E145")])],"isStart":false});
            var Q4;
            Q4=makeQuery(id+"F22.opExtrude","CAP_EDGE",EDGE,{"disambiguationData":[OSD([sQuery(id+"F16.wireOp",EDGE,"E153")])],"isStart":false});
            var Q5;
            Q5=makeQuery(id+"F22.opExtrude","CAP_EDGE",EDGE,{"disambiguationData":[OSD([sQuery(id+"F16.wireOp",EDGE,"E154")])],"isStart":false});
            var Q6;
            Q6=makeQuery(id+"F22.opExtrude","CAP_EDGE",EDGE,{"disambiguationData":[OSD([sQuery(id+"F16.wireOp",EDGE,"E151")])],"isStart":false});
            fillet(context, id + "F28", {"entities" : qUnion([Q0, Q1, Q2, Q3, Q4, Q5, Q6]), "radius" : 0.5 * mm, "tangentPropagation" : true, "allowEdgeOverflow" : false});
        }
        {
            var Q0;
            {var subQ0=sQuery(id+"F0.wireOp",EDGE,"E8");Q0=makeQuery(id+"F4.boolean.opBoolean","MERGE",FACE,{"derivedFrom":[makeQuery(id+"F1.opExtrude","CAP_FACE",FACE,{"disambiguationData":[OSD([sQuery(id+"F0.wireOp",EDGE,"E0"),sQuery(id+"F0.wireOp",EDGE,"E1"),sQuery(id+"F0.wireOp",EDGE,"E2"),sQuery(id+"F0.wireOp",EDGE,"E3"),sQuery(id+"F0.wireOp",EDGE,"E4"),sQuery(id+"F0.wireOp",EDGE,"E5"),sQuery(id+"F0.wireOp",EDGE,"E6"),sQuery(id+"F0.wireOp",EDGE,"E7"),subQ0,sQuery(id+"F0.wireOp",EDGE,"E9"),sQuery(id+"F0.wireOp",EDGE,"E10"),sQuery(id+"F0.wireOp",EDGE,"E11"),sQuery(id+"F0.wireOp",EDGE,"E12"),sQuery(id+"F0.wireOp",EDGE,"E13"),sQuery(id+"F0.wireOp",EDGE,"E14"),sQuery(id+"F0.wireOp",EDGE,"E15")])],"isStart":false}),makeQuery(id+"F4.opRevolve","SWEPT_FACE",FACE,{"disambiguationData":[OSD([subQ0])]})]});}
            var sketch = newSketch(context, id + "F29", { "sketchPlane" : qUnion([Q0])});
            skText(sketch, "E161", { "text": "MedBox", "fontName": "OpenSans-Bold.ttf"});
            skPoint(sketch, "E161.firstSnap0", {"position": v(-8.08, 10.94) * mm});
            skLineSegment(sketch, "E162", {"start": v(-41, 0) * mm, "end": v(-45, 0) * mm});
            const initialGuessF29  = {"E161": [-0.041, 0.015, 0, -1, 0.00527]};
            skSetInitialGuess(sketch, initialGuessF29);
            skSolve(sketch);
        }
        {
            var Q0;
            Q0=makeQuery(id+"F29.imprint","IMPRINT",FACE,{"disambiguationData":[TD([[makeQuery(id+"F29.imprint","IMPRINT",EDGE,{"derivedFrom":sQuery(id+"F29.wireOp",EDGE,"E161.sketch_text.stroke-19")}),-1.0]])]});
            var Q1;
            Q1=makeQuery(id+"F29.imprint","IMPRINT",FACE,{"disambiguationData":[TD([[makeQuery(id+"F29.imprint","IMPRINT",EDGE,{"derivedFrom":sQuery(id+"F29.wireOp",EDGE,"E161.sketch_text.stroke-39")}),-1.0]])]});
            var Q2;
            Q2=makeQuery(id+"F29.imprint","IMPRINT",FACE,{"disambiguationData":[TD([[makeQuery(id+"F29.imprint","IMPRINT",EDGE,{"derivedFrom":sQuery(id+"F29.wireOp",EDGE,"E161.sketch_text.stroke-62")}),-1.0]])]});
            var Q3;
            Q3=makeQuery(id+"F29.imprint","IMPRINT",FACE,{"disambiguationData":[TD([[makeQuery(id+"F29.imprint","IMPRINT",EDGE,{"derivedFrom":sQuery(id+"F29.wireOp",EDGE,"E161.sketch_text.stroke-87")}),-1.0]])]});
            var Q4;
            Q4=makeQuery(id+"F29.imprint","IMPRINT",FACE,{"disambiguationData":[TD([[makeQuery(id+"F29.imprint","IMPRINT",EDGE,{"derivedFrom":sQuery(id+"F29.wireOp",EDGE,"E161.sketch_text.stroke-105")}),-1.0]])]});
            var Q5;
            Q5=makeQuery(id+"F29.imprint","IMPRINT",FACE,{"disambiguationData":[TD([[makeQuery(id+"F29.imprint","IMPRINT",EDGE,{"derivedFrom":sQuery(id+"F29.wireOp",EDGE,"E161.sketch_text.stroke-0")}),-1.0]])]});
            extrude(context, id + "F30", {"entities" : qUnion([Q0, Q1, Q2, Q3, Q4, Q5]), "operationType" : NewBodyOperationType.REMOVE, "oppositeDirection" : true, "depth" : .4 * mm, "offsetDistance" : 25 * mm});
        }
    });
